FREECAD ASSEMBLY — COMPONENT RECIPES ("row")

This assembly document has 14 components, labeled P0..P13 below (a component is one placed body or linked part). 12 of them carry a construction recipe — the FreeCAD feature program that regenerates the part from scratch, quoted from this document or its linked companion documents; the rest are supplied as boundary geometry only. No exploded tour is included for this assembly.
COMPONENT P0 — recipe-attached ("BusBoard", a linked part whose construction recipe lives in a companion FreeCAD document of the same project; that document's serialized recipe follows).
Construction recipe (the companion document, serialized — sketch geometry with constraints, then the solid features built on it; lengths are millimeters unless a unit is written):

FCSTD DOCUMENT  (FreeCAD 1.0R38641 +468 (Git))
Label: doepfer_bus_board_v6
License: All rights reserved
LicenseURL: https://en.wikipedia.org/wiki/All_rights_reserved
objects: Sketcher::SketchObject×1, PartDesign::Pad×1, PartDesign::Body×1
note: 6 computed .brp shape members not serialized (recipe doc carries the construction recipe); baked Part::Feature solids carry a one-line shape summary decoded from their .brp

FEATURE [Sketcher::SketchObject] Sketch
  ArcFitTolerance = 1e-06
  AttachmentSupport = -> [XY_Plane]
  FullyConstrained = true
  MakeInternals = false
  MapMode = 5
  sketch-geometry (19):
    g0: LineSegment StartX=0 StartY=41.91 StartZ=0 EndX=0 EndY=0 EndZ=0
    g1: LineSegment StartX=0 StartY=0 StartZ=0 EndX=391.16 EndY=0 EndZ=0
    g2: LineSegment StartX=391.16 StartY=0 StartZ=0 EndX=391.16 EndY=41.91 EndZ=0
    g3: LineSegment StartX=391.16 StartY=41.91 StartZ=0 EndX=0 EndY=41.91 EndZ=0
    g4: Circle CenterX=24.13 CenterY=3.175 CenterZ=0 NormalX=0 NormalY=0 NormalZ=1 AngleXU=0 Radius=1.5
    g5: Circle [constr] CenterX=49.53 CenterY=3.175 CenterZ=0 NormalX=0 NormalY=0 NormalZ=1 AngleXU=0 Radius=1.5
    g6: Circle CenterX=74.93 CenterY=3.175 CenterZ=0 NormalX=0 NormalY=0 NormalZ=1 AngleXU=0 Radius=1.5
    g7: Circle [constr] CenterX=100.33 CenterY=3.175 CenterZ=0 NormalX=0 NormalY=0 NormalZ=1 AngleXU=0 Radius=1.5
    g8: Circle CenterX=125.73 CenterY=3.175 CenterZ=0 NormalX=0 NormalY=0 NormalZ=1 AngleXU=0 Radius=1.5
    g9: Circle CenterX=176.53 CenterY=3.175 CenterZ=0 NormalX=0 NormalY=0 NormalZ=1 AngleXU=0 Radius=1.5
    g10: Circle [constr] CenterX=151.13 CenterY=3.175 CenterZ=0 NormalX=0 NormalY=0 NormalZ=1 AngleXU=0 Radius=1.5
    g11: LineSegment [constr] StartX=0 StartY=3.175 StartZ=0 EndX=391.16 EndY=3.175 EndZ=0
    g12: Circle CenterX=214.63 CenterY=3.175 CenterZ=0 NormalX=0 NormalY=0 NormalZ=1 AngleXU=0 Radius=1.5
    g13: Circle [constr] CenterX=240.03 CenterY=3.175 CenterZ=0 NormalX=0 NormalY=0 NormalZ=1 AngleXU=0 Radius=1.5
    g14: Circle CenterX=265.43 CenterY=3.175 CenterZ=0 NormalX=0 NormalY=0 NormalZ=1 AngleXU=0 Radius=1.5
    g15: Circle [constr] CenterX=290.83 CenterY=3.175 CenterZ=0 NormalX=0 NormalY=0 NormalZ=1 AngleXU=0 Radius=1.5
    g16: Circle CenterX=316.23 CenterY=3.175 CenterZ=0 NormalX=0 NormalY=0 NormalZ=1 AngleXU=0 Radius=1.5
    g17: Circle [constr] CenterX=341.63 CenterY=3.175 CenterZ=0 NormalX=0 NormalY=0 NormalZ=1 AngleXU=0 Radius=1.5
    g18: Circle CenterX=367.03 CenterY=3.175 CenterZ=0 NormalX=0 NormalY=0 NormalZ=1 AngleXU=0 Radius=1.5
  constraints (52):
    c: Coincident(g0,g1)
    c: Coincident(g1,g2)
    c: Coincident(g2,g3)
    c: Coincident(g3,g0)
    c: Vertical(g0)
    c: Vertical(g2)
    c: Horizontal(g1)
    c: Horizontal(g3)
    c: Coincident(g0,g-1)
    c: DistanceX(g1,g1) = 391.16
    c: DistanceY(g0,g0) = 41.91
    c: PointOnObject(g11,g0)
    c: PointOnObject(g11,g2)
    c: Horizontal(g11)
    c: DistanceY(g0,g11) = 3.175
    c: PointOnObject(g4,g11)
    c: PointOnObject(g5,g11)
    c: PointOnObject(g6,g11)
    c: PointOnObject(g7,g11)
    c: PointOnObject(g8,g11)
    c: PointOnObject(g9,g11)
    c: PointOnObject(g10,g11)
    c: DistanceX(g11,g4) = 24.13
    c: DistanceX(g4,g5) = 25.4
    c: DistanceX(g5,g6) = 25.4
    c: DistanceX(g6,g7) = 25.4
    c: Distance(g7,g8) = 25.4
    c: Distance(g8,g10) = 25.4
    c: DistanceX(g10,g9) = 25.4
    c: PointOnObject(g12,g11)
    c: PointOnObject(g13,g11)
    c: PointOnObject(g14,g11)
    c: PointOnObject(g15,g11)
    c: PointOnObject(g16,g11)
    c: PointOnObject(g17,g11)
    c: PointOnObject(g18,g11)
    c: DistanceX(g9,g12) = 38.1
    c: DistanceX(g12,g13) = 25.4
    c: DistanceX(g13,g14) = 25.4
    c: DistanceX(g14,g15) = 25.4
    c: DistanceX(g15,g16) = 25.4
    c: DistanceX(g16,g17) = 25.4
    c: DistanceX(g17,g18) = 25.4
    c: Diameter(g4) = 3  'HoleDiameter'
    c: Equal(g4, g5-g8) x4
    c: Equal(g4,g10)
    c: Equal(g4,g9)
    c: Equal(g4, g12-g15) x4
    c: Equal(g16,g4)
    c: Equal(g4,g17)
    c: Equal(g18,g4)
    c: DistanceX(g18,g11) = 24.13
FEATURE [PartDesign::Pad] Pad
  Direction = (0,0,1)
  Length = 1
  Length2 = 10
  Profile = -> Sketch
  ReferenceAxis = -> Sketch [N_Axis]
  Refine = true
  Suppressed = false
  Type = 0
FEATURE [PartDesign::Body] Body  label="BusBoard"
  AllowCompound = false
  Group = -> [Sketch,Pad]
  Origin = -> Origin
  Tip = -> Pad
COMPONENT P1 — recipe-attached ("FrameBracket", a linked part whose construction recipe lives in a companion FreeCAD document of the same project; that document's serialized recipe follows).
Construction recipe (the companion document, serialized — sketch geometry with constraints, then the solid features built on it; lengths are millimeters unless a unit is written):

FCSTD DOCUMENT  (FreeCAD 1.0R38641 +468 (Git))
Label: frame_bracket
License: All rights reserved
LicenseURL: https://en.wikipedia.org/wiki/All_rights_reserved
objects: PartDesign::SubShapeBinder×1, Sketcher::SketchObject×1, PartDesign::Pad×1, PartDesign::Body×1
note: 7 computed .brp shape members not serialized (recipe doc carries the construction recipe); baked Part::Feature solids carry a one-line shape summary decoded from their .brp
EXTERNAL_REF file=panel_side.FCStd obj=Body001
EXTERNAL_REF file=dimensions.FCStd obj=VarSet

FEATURE [PartDesign::SubShapeBinder] Binder  label="SidePanelBinder"
  BindCopyOnChange = 0
  BindMode = 0
  ClaimChildren = false
  Context = -> Body [Binder.]
  Fuse = false
  MakeFace = true
  OffsetFill = false
  OffsetIntersection = false
  OffsetJoinType = 0
  OffsetOpenResult = false
  PartialLoad = false
  Refine = true
  Relative = true
  Support = -> [<external panel_side.FCStd>#Body001]
  _Version = 2
FEATURE [Sketcher::SketchObject] Sketch
  ArcFitTolerance = 1e-06
  AttachmentSupport = -> [Binder]
  ExternalGeometry = -> [Binder]
  FullyConstrained = true
  MakeInternals = false
  MapMode = 5
  Placement = pos=(-1.8542,0,0) rot=(0.57735,0.57735,0.57735;2.0944rad)
  expr: Constraints[114] = dimensions#VarSet.MaxAngle / 2
  expr: Constraints[115] = dimensions#VarSet.MaxAngle / 2
  expr: Constraints[63] = dimensions#VarSet.FrameHoleDiameter
  sketch-geometry (47):
    g0: Circle CenterX=56.923 CenterY=-56.25 CenterZ=0 NormalX=0 NormalY=0 NormalZ=1 AngleXU=0 Radius=3
    g1: Circle CenterX=73.177 CenterY=-56.25 CenterZ=0 NormalX=0 NormalY=0 NormalZ=1 AngleXU=0 Radius=3
    g2: ArcOfCircle CenterX=56.923 CenterY=-56.25 CenterZ=0 NormalX=0 NormalY=0 NormalZ=1 AngleXU=0 Radius=8 StartAngle=3.09569 EndAngle=4.71239
    g3: ArcOfCircle CenterX=73.177 CenterY=-56.25 CenterZ=0 NormalX=0 NormalY=0 NormalZ=1 AngleXU=0 Radius=8 StartAngle=6.23728 EndAngle=7.85398
    g4: ArcOfCircle CenterX=4.7e-14 CenterY=11.2 CenterZ=0 NormalX=0 NormalY=0 NormalZ=1 AngleXU=0 Radius=18.527 StartAngle=3.14159 EndAngle=3.33794
    g5: ArcOfCircle CenterX=-10.527 CenterY=11.2 CenterZ=0 NormalX=0 NormalY=0 NormalZ=1 AngleXU=0 Radius=8 StartAngle=6.23728 EndAngle=9.42478
    g6: ArcOfCircle CenterX=4.7e-14 CenterY=11.2 CenterZ=0 NormalX=0 NormalY=0 NormalZ=1 AngleXU=0 Radius=13.527 StartAngle=3.14159 EndAngle=3.33794
    g7: ArcOfCircle CenterX=-10.3247 CenterY=9.14628 CenterZ=0 NormalX=0 NormalY=0 NormalZ=1 AngleXU=0 Radius=3 StartAngle=3.33794 EndAngle=6.47953
    g8: ArcOfCircle CenterX=-10.527 CenterY=11.2 CenterZ=0 NormalX=0 NormalY=0 NormalZ=1 AngleXU=0 Radius=3 StartAngle=0 EndAngle=3.14159
    g9: ArcOfCircle CenterX=4.7e-14 CenterY=11.2 CenterZ=0 NormalX=0 NormalY=0 NormalZ=1 AngleXU=0 Radius=7.527 StartAngle=3.14159 EndAngle=3.33794
    g10: ArcOfCircle CenterX=4.67e-14 CenterY=-123.7 CenterZ=0 NormalX=0 NormalY=0 NormalZ=1 AngleXU=0 Radius=148.627 StartAngle=6.08684 EndAngle=6.28319
    g11: ArcOfCircle CenterX=137.925 CenterY=-151.135 CenterZ=0 NormalX=0 NormalY=0 NormalZ=1 AngleXU=0 Radius=8 StartAngle=2.94524 EndAngle=6.08684
    g12: ArcOfCircle CenterX=4.67e-14 CenterY=-123.7 CenterZ=0 NormalX=0 NormalY=0 NormalZ=1 AngleXU=0 Radius=132.627 StartAngle=6.08684 EndAngle=6.28648
    g13: ArcOfCircle CenterX=4.67e-14 CenterY=-123.7 CenterZ=0 NormalX=0 NormalY=0 NormalZ=1 AngleXU=0 Radius=143.627 StartAngle=6.08684 EndAngle=6.28319
    g14: ArcOfCircle CenterX=140.627 CenterY=-123.7 CenterZ=0 NormalX=0 NormalY=0 NormalZ=1 AngleXU=0 Radius=3 StartAngle=3e-16 EndAngle=3.14159
    g15: ArcOfCircle CenterX=137.925 CenterY=-151.135 CenterZ=0 NormalX=0 NormalY=0 NormalZ=1 AngleXU=0 Radius=3 StartAngle=2.94524 EndAngle=6.08684
    g16: ArcOfCircle CenterX=4.67e-14 CenterY=-123.7 CenterZ=0 NormalX=0 NormalY=0 NormalZ=1 AngleXU=0 Radius=137.627 StartAngle=6.08684 EndAngle=6.28319
    g17: LineSegment [constr] StartX=4.67e-14 StartY=-123.7 StartZ=0 EndX=148.627 EndY=-123.7 EndZ=0
    g18: LineSegment [constr] StartX=4.7e-14 StartY=11.2 StartZ=0 EndX=-18.527 EndY=11.2 EndZ=0
    g19: LineSegment [constr] StartX=56.923 StartY=-56.25 StartZ=0 EndX=-10.527 EndY=11.2 EndZ=0
    g20: LineSegment [constr] StartX=73.177 StartY=-56.25 StartZ=0 EndX=140.627 EndY=-123.7 EndZ=0
    g21: LineSegment [constr] StartX=73.177 StartY=-59.25 StartZ=0 EndX=76.177 EndY=-59.25 EndZ=0
    g22: LineSegment StartX=81.5188 StartY=-57.5207 StartZ=0 EndX=139.356 EndY=-115.358 EndZ=0
    g23: LineSegment StartX=74.4574 StartY=-64.6015 StartZ=0 EndX=132.275 EndY=-122.419 EndZ=0
    g24: LineSegment StartX=-7.42456 StartY=1.02649 StartZ=0 EndX=48.5812 EndY=-54.9793 EndZ=0
    g25: LineSegment StartX=55.6426 StartY=-47.8985 StartZ=0 EndX=-2.18522 EndY=9.92929 EndZ=0
    g26: ArcOfCircle CenterX=47.7327 CenterY=-55.8278 CenterZ=0 NormalX=0 NormalY=0 NormalZ=1 AngleXU=0 Radius=1.2 StartAngle=6.23728 EndAngle=7.06858
    g27: LineSegment StartX=56.4911 StartY=-48.25 StartZ=0 EndX=73.177 EndY=-48.25 EndZ=0
    g28: ArcOfCircle CenterX=56.4911 CenterY=-47.05 CenterZ=0 NormalX=0 NormalY=0 NormalZ=1 AngleXU=0 Radius=1.2 StartAngle=3.92699 EndAngle=4.71239
    g29: ArcOfCircle CenterX=82.3673 CenterY=-56.6722 CenterZ=0 NormalX=0 NormalY=0 NormalZ=1 AngleXU=0 Radius=1.2 StartAngle=3.09569 EndAngle=3.92699
    g30: ArcOfCircle CenterX=73.6089 CenterY=-65.45 CenterZ=0 NormalX=0 NormalY=0 NormalZ=1 AngleXU=0 Radius=1.2 StartAngle=0.785398 EndAngle=1.5708
    g31: LineSegment StartX=56.923 StartY=-64.25 StartZ=0 EndX=73.6089 EndY=-64.25 EndZ=0
    g32: ArcOfCircle CenterX=140.627 CenterY=-123.7 CenterZ=0 NormalX=0 NormalY=0 NormalZ=1 AngleXU=0 Radius=8 StartAngle=2e-16 EndAngle=1.6167
    g33: ArcOfCircle CenterX=140.205 CenterY=-114.51 CenterZ=0 NormalX=0 NormalY=0 NormalZ=1 AngleXU=0 Radius=1.2 StartAngle=3.92699 EndAngle=4.75829
    g34: ArcOfCircle CenterX=131.426 CenterY=-123.267 CenterZ=0 NormalX=0 NormalY=0 NormalZ=1 AngleXU=0 Radius=1.2 StartAngle=0.00329147 EndAngle=0.785398
    g35: ArcOfCircle CenterX=-10.3247 CenterY=9.14628 CenterZ=0 NormalX=0 NormalY=0 NormalZ=1 AngleXU=0 Radius=8 StartAngle=3.33794 EndAngle=4.93728
    g36: ArcOfCircle CenterX=-8.27309 CenterY=0.177963 CenterZ=0 NormalX=0 NormalY=0 NormalZ=1 AngleXU=0 Radius=1.2 StartAngle=0.785398 EndAngle=1.79569
    g37: ArcOfCircle CenterX=-1.33669 CenterY=10.7778 CenterZ=0 NormalX=0 NormalY=0 NormalZ=1 AngleXU=0 Radius=1.2 StartAngle=3.09569 EndAngle=3.92699
    g38: LineSegment [constr] StartX=4.7e-14 StartY=11.2 StartZ=0 EndX=4.7e-14 EndY=10 EndZ=0
    g39: LineSegment [constr] StartX=4.67e-14 StartY=-123.7 StartZ=0 EndX=4.67e-14 EndY=-122.5 EndZ=0
    g40: LineSegment [constr] StartX=53.923 StartY=-53.25 StartZ=0 EndX=56.923 EndY=-53.25 EndZ=0
    g41: LineSegment [constr] StartX=56.923 StartY=-53.25 StartZ=0 EndX=56.923 EndY=-56.25 EndZ=0
    g42: LineSegment [constr] StartX=73.177 StartY=-56.25 StartZ=0 EndX=73.177 EndY=-59.25 EndZ=0
    g43: LineSegment [constr] StartX=103.366 StartY=-93.5105 StartZ=0 EndX=106.902 EndY=-89.975 EndZ=0
    g44: LineSegment [constr] StartX=106.902 StartY=-89.975 StartZ=0 EndX=110.438 EndY=-86.4395 EndZ=0
    g45: LineSegment [constr] StartX=19.6625 StartY=-26.0605 StartZ=0 EndX=23.198 EndY=-22.525 EndZ=0
    g46: LineSegment [constr] StartX=23.198 StartY=-22.525 StartZ=0 EndX=26.7335 EndY=-18.9895 EndZ=0
  constraints (116):
    c: Coincident(g2,g0)
    c: Coincident(g3,g1)
    c: Tangent(g4,g5) = -1.5708
    c: Tangent(g4,g35) = -1.5708
    c: Coincident(g6,g9)
    c: Tangent(g9,g8) = 1.5708
    c: Tangent(g9,g7) = 1.5708
    c: Tangent(g6,g8) = -1.5708
    c: Tangent(g6,g7) = -1.5708
    c: Coincident(g6,g4)
    c: Coincident(g7,g35)
    c: Coincident(g10,g12)
    c: Tangent(g12,g11) = 1.5708
    c: Tangent(g10,g32) = -1.5708
    c: Tangent(g10,g11) = -1.5708
    c: Coincident(g13,g16)
    c: Tangent(g16,g15) = 1.5708
    c: Tangent(g16,g14) = 1.5708
    c: Tangent(g13,g15) = -1.5708
    c: Tangent(g13,g14) = -1.5708
    c: Coincident(g13,g10)
    c: Coincident(g14,g32)
    c: Coincident(g17,g10)
    c: Equal(g0,g1)
    c: Equal(g1,g14)
    c: Equal(g7,g0)
    c: Coincident(g18,g4)
    c: Horizontal(g18)
    c: Coincident(g4,g18)
    c: Coincident(g19,g0)
    c: Coincident(g5,g19)
    c: Coincident(g20,g1)
    c: PointOnObject(g21,g1)
    c: PointOnObject(g21,g20)
    c: Horizontal(g21)
    c: Coincident(g20,g32)
    c: Parallel(g23,g20)
    c: Parallel(g20,g22)
    c: Parallel(g24,g19)
    c: Parallel(g19,g25)
    c: Tangent(g26,g2) = 1.5708
    c: Tangent(g24,g26) = 1.5708
    c: Horizontal(g27)
    c: Tangent(g28,g27) = -1.5708
    c: Tangent(g25,g28) = 1.5708
    c: Tangent(g29,g3) = 1.5708
    c: Tangent(g29,g22) = -1.5708
    c: Tangent(g23,g30) = 1.5708
    c: Horizontal(g31)
    c: Tangent(g3,g27) = 1.5708
    c: Tangent(g2,g31) = -1.5708
    c: Distance(g25,g24) = 10
    c: Distance(g22,g23) = 10
    c: Tangent(g30,g31) = 1.5708
    c: Tangent(g33,g32) = 1.5708
    c: Tangent(g33,g22) = -1.5708
    c: Tangent(g34,g23) = 1.5708
    c: Coincident(g17,g10)
    c: Tangent(g35,g36) = 1.5708
    c: Tangent(g36,g24) = 1.5708
    c: Tangent(g37,g25) = 1.5708
    c: Coincident(g8,g5)
    c: Tangent(g12,g34) = -1.5708
    c: Diameter(g0) = 6
    c: Coincident(g38,g4)
    c: Coincident(g39,g10)
    c: Horizontal(g17)
    c: Coincident(g15,g11)
    c: Equal(g39,g38)
    c: Distance(g2,g0) = 5
    c: Equal(g2,g3)
    c: Equal(g29,g30)
    c: Equal(g30,g26)
    c: Equal(g28,g26)
    c: Distance(g15,g11) = 5
    c: Distance(g5,g8) = 5
    c: Distance(g38,g38) = 1.2
    c: Tangent(g37,g5) = 1.5708
    c: Equal(g34,g33)
    c: Equal(g33,g30)
    c: PointOnObject(g40,g19)
    c: PointOnObject(g40,g0)
    c: Horizontal(g40)
    c: Coincident(g41,g40)
    c: Coincident(g41,g0)
    c: Vertical(g41)
    c: Equal(g41,g40)
    c: Coincident(g42,g1)
    c: Coincident(g42,g21)
    c: Vertical(g42)
    c: Equal(g42,g21)
    c: Equal(g28,g37)
    c: Equal(g37,g36)
    c: Radius(g30) = 1.2
    c: PointOnObject(g43,g23)
    c: Coincident(g44,g43)
    c: PointOnObject(g44,g22)
    c: Perpendicular(g43,g23)
    c: Perpendicular(g22,g44)
    c: Equal(g43,g44)
    c: PointOnObject(g45,g24)
    c: PointOnObject(g46,g25)
    c: Perpendicular(g25,g46)
    c: Perpendicular(g24,g45)
    c: Coincident(g46,g45)
    c: Equal(g46,g45)
    c: Symmetric(g1,g14,g43)
    c: Symmetric(g0,g5,g45)
    c: Coincident(g1,g-4)
    c: Coincident(g0,g-3)
    c: Coincident(g39,g-5)
    c: Vertical(g39)
    c: Coincident(g38,g-6)
    c: Vertical(g38)
    c: Angle(g10) = 0.19635
    c: Angle(g4) = 0.19635
FEATURE [PartDesign::Pad] Pad
  Direction = (1,0,0)
  Length = 3.175
  Length2 = 10
  Profile = -> Sketch
  ReferenceAxis = -> Sketch [N_Axis]
  Refine = true
  Reversed = true
  Suppressed = false
  Type = 0
  expr: Length = <<dimensions>>#VarSet.FrameTotalThickness
FEATURE [PartDesign::Body] Body  label="FrameBracket"
  AllowCompound = false
  Group = -> [Sketch,Pad,Binder]
  Origin = -> Origin
  Tip = -> Pad
COMPONENT P2 — same part as P1; its construction recipe is shown at P1.
COMPONENT P3 — same part as P1; its construction recipe is shown at P1.
COMPONENT P4 — same part as P1; its construction recipe is shown at P1.
COMPONENT P5 — recipe-attached ("FramePanelSpacer", a linked part whose construction recipe lives in a companion FreeCAD document of the same project; that document's serialized recipe follows).
Construction recipe (the companion document, serialized — sketch geometry with constraints, then the solid features built on it; lengths are millimeters unless a unit is written):

FCSTD DOCUMENT  (FreeCAD 1.0R38641 +468 (Git))
Label: frame_panel_spacer
License: All rights reserved
LicenseURL: https://en.wikipedia.org/wiki/All_rights_reserved
objects: PartDesign::SubShapeBinder×2, Sketcher::SketchObject×1, PartDesign::Pad×1, PartDesign::Body×1
note: 8 computed .brp shape members not serialized (recipe doc carries the construction recipe); baked Part::Feature solids carry a one-line shape summary decoded from their .brp
EXTERNAL_REF file=panel_side.FCStd obj=Body001
EXTERNAL_REF file=dimensions.FCStd obj=VarSet
EXTERNAL_REF file=frame_bracket.FCStd obj=Body

FEATURE [PartDesign::SubShapeBinder] Binder  label="SidePanelBinder"
  BindCopyOnChange = 0
  BindMode = 0
  ClaimChildren = false
  Context = -> Body [Binder.]
  Fuse = false
  MakeFace = true
  OffsetFill = false
  OffsetIntersection = false
  OffsetJoinType = 0
  OffsetOpenResult = false
  PartialLoad = false
  Refine = true
  Relative = true
  Support = -> [<external panel_side.FCStd>#Body001]
  _Version = 2
FEATURE [PartDesign::SubShapeBinder] Binder001  label="BracketBinder"
  BindCopyOnChange = 0
  BindMode = 0
  ClaimChildren = false
  Context = -> Body [Binder001.]
  Fuse = false
  MakeFace = true
  OffsetFill = false
  OffsetIntersection = false
  OffsetJoinType = 0
  OffsetOpenResult = false
  PartialLoad = false
  Refine = true
  Relative = true
  Support = -> [<external frame_bracket.FCStd>#Body]
  _Version = 2
FEATURE [Sketcher::SketchObject] Sketch
  ArcFitTolerance = 1e-06
  AttachmentSupport = -> [Binder]
  ExternalGeometry = -> [Binder,Binder001]
  FullyConstrained = true
  MakeInternals = false
  MapMode = 5
  Placement = pos=(-1.8542,0,0) rot=(0.57735,0.57735,0.57735;2.0944rad)
  expr: Constraints[32] = dimensions#VarSet.FrameMinWidth
  expr: Constraints[33] = dimensions#VarSet.EnclosureCornerRadius
  expr: Constraints[41] = dimensions#VarSet.FrameHoleDiameter
  expr: Constraints[42] = dimensions#VarSet.FrameHoleDiameter / 2 + dimensions#VarSet.FrameMinWidth / 2
  sketch-geometry (21):
    g0: ArcOfCircle CenterX=56.923 CenterY=-56.25 CenterZ=0 NormalX=0 NormalY=0 NormalZ=1 AngleXU=0 Radius=8 StartAngle=1.5708 EndAngle=4.71239
    g1: ArcOfCircle CenterX=73.177 CenterY=-56.25 CenterZ=0 NormalX=0 NormalY=0 NormalZ=1 AngleXU=0 Radius=8 StartAngle=0.739492 EndAngle=1.5708
    g2: ArcOfCircle CenterX=79.9741 CenterY=-50.05 CenterZ=0 NormalX=0 NormalY=0 NormalZ=1 AngleXU=0 Radius=1.2 StartAngle=3.88109 EndAngle=4.71239
    g3: ArcOfCircle CenterX=73.177 CenterY=-56.25 CenterZ=0 NormalX=0 NormalY=0 NormalZ=1 AngleXU=0 Radius=8 StartAngle=4.71239 EndAngle=5.54369
    g4: ArcOfCircle CenterX=79.9741 CenterY=-62.45 CenterZ=0 NormalX=0 NormalY=0 NormalZ=1 AngleXU=0 Radius=1.2 StartAngle=1.5708 EndAngle=2.4021
    g5: ArcOfCircle CenterX=140.627 CenterY=-56.25 CenterZ=0 NormalX=0 NormalY=0 NormalZ=1 AngleXU=0 Radius=8 StartAngle=3.88109 EndAngle=8.68529
    g6: ArcOfCircle CenterX=133.83 CenterY=-62.45 CenterZ=0 NormalX=0 NormalY=0 NormalZ=1 AngleXU=0 Radius=1.2 StartAngle=0.739492 EndAngle=1.5708
    g7: ArcOfCircle CenterX=133.83 CenterY=-50.05 CenterZ=0 NormalX=0 NormalY=0 NormalZ=1 AngleXU=0 Radius=1.2 StartAngle=4.71239 EndAngle=5.54369
    g8: LineSegment StartX=56.923 StartY=-48.25 StartZ=0 EndX=73.177 EndY=-48.25 EndZ=0
    g9: LineSegment StartX=56.923 StartY=-64.25 StartZ=0 EndX=73.177 EndY=-64.25 EndZ=0
    g10: LineSegment StartX=79.9741 StartY=-61.25 StartZ=0 EndX=133.83 EndY=-61.25 EndZ=0
    g11: LineSegment StartX=79.9741 StartY=-51.25 StartZ=0 EndX=133.83 EndY=-51.25 EndZ=0
    g12: LineSegment [constr] StartX=56.923 StartY=-56.25 StartZ=0 EndX=140.627 EndY=-56.25 EndZ=0
    g13: LineSegment [constr] StartX=56.923 StartY=-48.25 StartZ=0 EndX=56.923 EndY=-64.25 EndZ=0
    g14: LineSegment [constr] StartX=73.177 StartY=-48.25 StartZ=0 EndX=73.177 EndY=-64.25 EndZ=0
    g15: Circle CenterX=56.923 CenterY=-56.25 CenterZ=0 NormalX=0 NormalY=0 NormalZ=1 AngleXU=0 Radius=3
    g16: Circle CenterX=73.177 CenterY=-56.25 CenterZ=0 NormalX=0 NormalY=0 NormalZ=1 AngleXU=0 Radius=3
    g17: Circle CenterX=140.627 CenterY=-56.25 CenterZ=0 NormalX=0 NormalY=0 NormalZ=1 AngleXU=0 Radius=3
    g18: LineSegment [constr] StartX=148.627 StartY=-123.7 StartZ=0 EndX=148.627 EndY=-56.25 EndZ=0
    g19: Circle [constr] CenterX=56.923 CenterY=-56.25 CenterZ=0 NormalX=0 NormalY=0 NormalZ=1 AngleXU=0 Radius=8
    g20: Circle [constr] CenterX=73.177 CenterY=-56.25 CenterZ=0 NormalX=0 NormalY=0 NormalZ=1 AngleXU=0 Radius=8
  constraints (51):
    c: Coincident(g3,g1)
    c: Coincident(g8,g0)
    c: Coincident(g8,g1)
    c: Horizontal(g8)
    c: Coincident(g9,g0)
    c: Coincident(g9,g3)
    c: Horizontal(g9)
    c: Horizontal(g11)
    c: Horizontal(g10)
    c: Tangent(g4,g3) = 1.5708
    c: Tangent(g2,g1) = 1.5708
    c: Tangent(g7,g5) = 1.5708
    c: Tangent(g5,g6) = 1.5708
    c: Coincident(g12,g0)
    c: Coincident(g12,g5)
    c: Horizontal(g12)
    c: Coincident(g13,g0)
    c: Coincident(g13,g0)
    c: Vertical(g13)
    c: PointOnObject(g0,g13)
    c: Coincident(g14,g1)
    c: Coincident(g14,g3)
    c: PointOnObject(g1,g14)
    c: Vertical(g14)
    c: Tangent(g11,g2) = -1.5708
    c: Tangent(g10,g4) = 1.5708
    c: Tangent(g7,g11) = -1.5708
    c: Tangent(g10,g6) = 1.5708
    c: Equal(g1,g5)
    c: Equal(g2,g7)
    c: Equal(g6,g4)
    c: Symmetric(g4,g2,g12)
    c: Distance(g10,g11) = 10
    c: Radius(g2) = 1.2
    c: Coincident(g0,g-3)
    c: Coincident(g1,g-4)
    c: Coincident(g15,g0)
    c: Coincident(g16,g1)
    c: Coincident(g17,g5)
    c: Equal(g17,g16)
    c: Equal(g16,g15)
    c: Diameter(g15) = 6
    c: Radius(g0) = 8
    c: Vertical(g18)
    c: Coincident(g-5,g18)
    c: Tangent(g18,g5) = -1.5708
    c: Coincident(g19,g0)
    c: Equal(g19,g0)
    c: Coincident(g20,g1)
    c: Equal(g20,g1)
    c: Distance(g19,g20) = 0.254
FEATURE [PartDesign::Pad] Pad
  Direction = (1,0,0)
  Length = 3.175
  Length2 = 10
  Profile = -> Sketch
  ReferenceAxis = -> Sketch [N_Axis]
  Refine = true
  Reversed = true
  Suppressed = false
  Type = 0
  expr: Length = <<dimensions>>#VarSet.FrameTotalThickness
FEATURE [PartDesign::Body] Body  label="FramePanelSpacer"
  AllowCompound = false
  Group = -> [Pad,Sketch,Binder,Binder001]
  Origin = -> Origin
  Tip = -> Pad
COMPONENT P6 — same part as P5; its construction recipe is shown at P5.
COMPONENT P7 — recipe-attached ("PanelBack", a linked part whose construction recipe lives in a companion FreeCAD document of the same project; that document's serialized recipe follows).
Construction recipe (the companion document, serialized — sketch geometry with constraints, then the solid features built on it; lengths are millimeters unless a unit is written):

FCSTD DOCUMENT  (FreeCAD 1.0R38641 +468 (Git))
Label: panel_back
License: All rights reserved
LicenseURL: https://en.wikipedia.org/wiki/All_rights_reserved
objects: PartDesign::SubShapeBinder×4, Sketcher::SketchObject×1, PartDesign::Pad×1, PartDesign::Body×1
note: 10 computed .brp shape members not serialized (recipe doc carries the construction recipe); baked Part::Feature solids carry a one-line shape summary decoded from their .brp
EXTERNAL_REF file=dimensions.FCStd obj=VarSet
EXTERNAL_REF file=../third_party/doepfer_bus_board_v6.FCStd obj=Sketch
EXTERNAL_REF file=panel_top_and_bottom.FCStd obj=Body
EXTERNAL_REF file=panel_side.FCStd obj=Body001
EXTERNAL_REF file=../third_party/doepfer_bus_board_v6.FCStd obj=Body
EXTERNAL_REF file=../third_party/doepfer_psu3.FCStd obj=Body

FEATURE [PartDesign::SubShapeBinder] Binder  label="BottomPanelBinder"
  BindCopyOnChange = 0
  BindMode = 0
  ClaimChildren = false
  Context = -> Body [Binder.]
  Fuse = false
  MakeFace = true
  OffsetFill = false
  OffsetIntersection = false
  OffsetJoinType = 0
  OffsetOpenResult = false
  PartialLoad = false
  Refine = true
  Relative = true
  Support = -> [<external panel_top_and_bottom.FCStd>#Body[Pad.]]
  _Version = 2
FEATURE [PartDesign::SubShapeBinder] Binder001  label="SidePanelBinder"
  BindCopyOnChange = 0
  BindMode = 0
  ClaimChildren = false
  Context = -> Body [Binder001.]
  Fuse = false
  MakeFace = true
  OffsetFill = false
  OffsetIntersection = false
  OffsetJoinType = 0
  OffsetOpenResult = false
  PartialLoad = false
  Refine = true
  Relative = true
  Support = -> [<external panel_side.FCStd>#Body001]
  _Version = 2
FEATURE [PartDesign::SubShapeBinder] Binder002  label="BusBoardBinder"
  BindCopyOnChange = 0
  BindMode = 0
  ClaimChildren = false
  Context = -> Body [Binder002.]
  Fuse = false
  MakeFace = true
  OffsetFill = false
  OffsetIntersection = false
  OffsetJoinType = 0
  OffsetOpenResult = false
  PartialLoad = false
  Placement = pos=(0,0,0) rot=(1,0,0;1.5708rad)
  Refine = true
  Relative = true
  Support = -> [<external ../third_party/doepfer_bus_board_v6.FCStd>#Body]
  _Version = 2
FEATURE [PartDesign::SubShapeBinder] Binder003  label="PsuBinder"
  BindCopyOnChange = 0
  BindMode = 0
  ClaimChildren = false
  Context = -> Body [Binder003.]
  Fuse = false
  MakeFace = true
  OffsetFill = false
  OffsetIntersection = false
  OffsetJoinType = 0
  OffsetOpenResult = false
  PartialLoad = false
  Placement = pos=(0,0,0) rot=(1,0,0;1.5708rad)
  Refine = true
  Relative = false
  Support = -> [<external ../third_party/doepfer_psu3.FCStd>#Body]
  _Version = 2
FEATURE [Sketcher::SketchObject] Sketch
  ArcFitTolerance = 1e-06
  AttachmentOffset = pos=(0,0,0.127) rot=(0,0,1;0rad)
  AttachmentSupport = -> [Binder001,Binder]
  ExternalGeometry = -> [Binder001,Binder,Binder002,Binder003]
  FullyConstrained = true
  MakeInternals = false
  MapMode = 5
  Placement = pos=(0,127.227,2.68e-14) rot=(1,0,0;1.5708rad)
  expr: .AttachmentOffset.Base.z = dimensions#VarSet.EnclosureFinishThickness
  expr: Constraints[189] = dimensions#VarSet.EnclosureFinishThickness
  expr: Constraints[288] = doepfer_bus_board_v6#Sketch.Constraints.HoleDiameter + 2 * dimensions#VarSet.EnclosureFinishThickness
  expr: Constraints[41] = 2 * <<dimensions>>#VarSet.EnclosureFinishThickness
  expr: Constraints[47] = dimensions#VarSet.EnclosureCornerRadius
  expr: Constraints[82] = <<dimensions>>#VarSet.FrameTotalThickness - 2 * <<dimensions>>#VarSet.EnclosureFinishThickness
  expr: Constraints[83] = dimensions#VarSet.FrameMinWidth + dimensions#VarSet.FrameHoleDiameter + 2 * dimensions#VarSet.FrameFinishThickness
  expr: Constraints[84] = dimensions#VarSet.FrameTotalThickness + 2 * dimensions#VarSet.EnclosureFinishThickness
  sketch-geometry (148):
    g0: LineSegment [constr] StartX=1e-15 StartY=-23.125 StartZ=0 EndX=1e-15 EndY=-23.379 EndZ=0
    g1: LineSegment [constr] StartX=9e-16 StartY=-89.121 StartZ=0 EndX=9e-16 EndY=-89.375 EndZ=0
    g2: LineSegment StartX=1e-15 StartY=-23.379 StartZ=0 EndX=-6.8772 EndY=-23.379 EndZ=0
    g3: LineSegment StartX=-8.0772 StartY=-24.579 StartZ=0 EndX=-8.0772 EndY=-87.921 EndZ=0
    g4: LineSegment StartX=-6.8772 StartY=-89.121 StartZ=0 EndX=9e-16 EndY=-89.121 EndZ=0
    g5: LineSegment StartX=1.2 StartY=-90.321 StartZ=0 EndX=1.2 EndY=-114.173 EndZ=0
    g6: LineSegment StartX=425.8 StartY=-114.173 StartZ=0 EndX=425.8 EndY=-90.321 EndZ=0
    g7: LineSegment StartX=427 StartY=-89.121 StartZ=0 EndX=433.877 EndY=-89.121 EndZ=0
    g8: LineSegment StartX=435.077 StartY=-87.921 StartZ=0 EndX=435.077 EndY=-24.579 EndZ=0
    g9: LineSegment StartX=433.877 StartY=-23.379 StartZ=0 EndX=427 EndY=-23.379 EndZ=0
    g10: LineSegment StartX=425.8 StartY=-22.179 StartZ=0 EndX=425.8 EndY=1.6729 EndZ=0
    g11: LineSegment StartX=1.2 StartY=1.6729 StartZ=0 EndX=1.2 EndY=-22.179 EndZ=0
    g12: ArcOfCircle CenterX=424.6 CenterY=1.6729 CenterZ=0 NormalX=0 NormalY=0 NormalZ=1 AngleXU=0 Radius=1.2 StartAngle=0 EndAngle=1.5708
    g13: ArcOfCircle CenterX=427 CenterY=-22.179 CenterZ=0 NormalX=0 NormalY=0 NormalZ=1 AngleXU=0 Radius=1.2 StartAngle=3.14159 EndAngle=4.71239
    g14: ArcOfCircle CenterX=433.877 CenterY=-24.579 CenterZ=0 NormalX=0 NormalY=0 NormalZ=1 AngleXU=0 Radius=1.2 StartAngle=8e-16 EndAngle=1.5708
    g15: ArcOfCircle CenterX=433.877 CenterY=-87.921 CenterZ=0 NormalX=0 NormalY=0 NormalZ=1 AngleXU=0 Radius=1.2 StartAngle=4.71239 EndAngle=6.28319
    g16: ArcOfCircle CenterX=427 CenterY=-90.321 CenterZ=0 NormalX=0 NormalY=0 NormalZ=1 AngleXU=0 Radius=1.2 StartAngle=1.5708 EndAngle=3.14159
    g17: ArcOfCircle CenterX=424.6 CenterY=-114.173 CenterZ=0 NormalX=0 NormalY=0 NormalZ=1 AngleXU=0 Radius=1.2 StartAngle=4.71239 EndAngle=6.28319
    g18: ArcOfCircle CenterX=2.4 CenterY=-114.173 CenterZ=0 NormalX=0 NormalY=0 NormalZ=1 AngleXU=0 Radius=1.2 StartAngle=3.14159 EndAngle=4.71239
    g19: ArcOfCircle CenterX=9e-16 CenterY=-90.321 CenterZ=0 NormalX=0 NormalY=0 NormalZ=1 AngleXU=0 Radius=1.2 StartAngle=2.6e-15 EndAngle=1.5708
    g20: ArcOfCircle CenterX=-6.8772 CenterY=-87.921 CenterZ=0 NormalX=0 NormalY=0 NormalZ=1 AngleXU=0 Radius=1.2 StartAngle=3.14159 EndAngle=4.71239
    g21: ArcOfCircle CenterX=-6.8772 CenterY=-24.579 CenterZ=0 NormalX=0 NormalY=0 NormalZ=1 AngleXU=0 Radius=1.2 StartAngle=1.5708 EndAngle=3.14159
    g22: ArcOfCircle CenterX=1.2e-15 CenterY=-22.179 CenterZ=0 NormalX=0 NormalY=0 NormalZ=1 AngleXU=0 Radius=1.2 StartAngle=4.71239 EndAngle=6.28319
    g23: ArcOfCircle CenterX=2.4 CenterY=1.6729 CenterZ=0 NormalX=0 NormalY=0 NormalZ=1 AngleXU=0 Radius=1.2 StartAngle=1.5708 EndAngle=3.14159
    g24: ArcOfCircle CenterX=-3.4417 CenterY=-48.25 CenterZ=0 NormalX=0 NormalY=0 NormalZ=1 AngleXU=0 Radius=1.7145 StartAngle=8e-16 EndAngle=3.14159
    g25: ArcOfCircle CenterX=-3.4417 CenterY=-64.25 CenterZ=0 NormalX=0 NormalY=0 NormalZ=1 AngleXU=0 Radius=1.7145 StartAngle=3.14159 EndAngle=6.28319
    g26: LineSegment StartX=-1.7272 StartY=-48.25 StartZ=0 EndX=-1.7272 EndY=-64.25 EndZ=0
    g27: LineSegment StartX=-5.1562 StartY=-48.25 StartZ=0 EndX=-5.1562 EndY=-64.25 EndZ=0
    g28: LineSegment [constr] StartX=-3.4417 StartY=-48.25 StartZ=0 EndX=-3.4417 EndY=-23.379 EndZ=0
    g29: LineSegment [constr] StartX=-3.4417 StartY=-64.25 StartZ=0 EndX=-3.4417 EndY=-89.121 EndZ=0
    g30: LineSegment [constr] StartX=430.442 StartY=-23.379 StartZ=0 EndX=430.442 EndY=-48.25 EndZ=0
    g31: LineSegment [constr] StartX=430.442 StartY=-89.121 StartZ=0 EndX=430.442 EndY=-64.25 EndZ=0
    g32: ArcOfCircle CenterX=430.442 CenterY=-48.25 CenterZ=0 NormalX=0 NormalY=0 NormalZ=1 AngleXU=0 Radius=1.7145 StartAngle=-1.8e-15 EndAngle=3.14159
    g33: ArcOfCircle CenterX=430.442 CenterY=-64.25 CenterZ=0 NormalX=0 NormalY=0 NormalZ=1 AngleXU=0 Radius=1.7145 StartAngle=3.14159 EndAngle=6.28319
    g34: LineSegment StartX=432.156 StartY=-48.25 StartZ=0 EndX=432.156 EndY=-64.25 EndZ=0
    g35: LineSegment StartX=428.727 StartY=-48.25 StartZ=0 EndX=428.727 EndY=-64.25 EndZ=0
    g36: LineSegment [constr] StartX=-8.0772 StartY=-48.25 StartZ=0 EndX=-5.1562 EndY=-48.25 EndZ=0
    g37: LineSegment [constr] StartX=432.156 StartY=-48.25 StartZ=0 EndX=435.077 EndY=-48.25 EndZ=0
    g38: LineSegment StartX=72.679 StartY=2.8729 StartZ=0 EndX=2.4 EndY=2.8729 EndZ=0
    g39: LineSegment StartX=139.621 StartY=4.0729 StartZ=0 EndX=139.621 EndY=5.9271 EndZ=0
    g40: LineSegment StartX=138.421 StartY=7.1271 StartZ=0 EndX=75.079 EndY=7.1271 EndZ=0
    g41: LineSegment StartX=73.879 StartY=5.9271 StartZ=0 EndX=73.879 EndY=4.0729 EndZ=0
    g42: ArcOfCircle CenterX=72.679 CenterY=4.0729 CenterZ=0 NormalX=0 NormalY=0 NormalZ=1 AngleXU=0 Radius=1.2 StartAngle=4.71239 EndAngle=6.28319
    g43: ArcOfCircle CenterX=75.079 CenterY=5.9271 CenterZ=0 NormalX=0 NormalY=0 NormalZ=1 AngleXU=0 Radius=1.2 StartAngle=1.5708 EndAngle=3.14159
    g44: ArcOfCircle CenterX=138.421 CenterY=5.9271 CenterZ=0 NormalX=0 NormalY=0 NormalZ=1 AngleXU=0 Radius=1.2 StartAngle=1e-16 EndAngle=1.5708
    g45: ArcOfCircle CenterX=140.821 CenterY=4.0729 CenterZ=0 NormalX=0 NormalY=0 NormalZ=1 AngleXU=0 Radius=1.2 StartAngle=3.14159 EndAngle=4.71239
    g46: LineSegment StartX=353.121 StartY=4.0729 StartZ=0 EndX=353.121 EndY=5.9271 EndZ=0
    g47: LineSegment StartX=351.921 StartY=7.1271 StartZ=0 EndX=288.579 EndY=7.1271 EndZ=0
    g48: LineSegment StartX=287.379 StartY=5.9271 StartZ=0 EndX=287.379 EndY=4.0729 EndZ=0
    g49: ArcOfCircle CenterX=286.179 CenterY=4.0729 CenterZ=0 NormalX=0 NormalY=0 NormalZ=1 AngleXU=0 Radius=1.2 StartAngle=4.71239 EndAngle=6.28319
    g50: ArcOfCircle CenterX=288.579 CenterY=5.9271 CenterZ=0 NormalX=0 NormalY=0 NormalZ=1 AngleXU=0 Radius=1.2 StartAngle=1.5708 EndAngle=3.14159
    g51: ArcOfCircle CenterX=351.921 CenterY=5.9271 CenterZ=0 NormalX=0 NormalY=0 NormalZ=1 AngleXU=0 Radius=1.2 StartAngle=3e-16 EndAngle=1.5708
    g52: ArcOfCircle CenterX=354.321 CenterY=4.0729 CenterZ=0 NormalX=0 NormalY=0 NormalZ=1 AngleXU=0 Radius=1.2 StartAngle=3.14159 EndAngle=4.71239
    g53: LineSegment StartX=424.6 StartY=2.8729 StartZ=0 EndX=354.321 EndY=2.8729 EndZ=0
    g54: LineSegment StartX=2.4 StartY=-115.373 StartZ=0 EndX=72.679 EndY=-115.373 EndZ=0
    g55: LineSegment StartX=73.879 StartY=-116.573 StartZ=0 EndX=73.879 EndY=-118.427 EndZ=0
    g56: LineSegment StartX=75.079 StartY=-119.627 StartZ=0 EndX=138.421 EndY=-119.627 EndZ=0
    g57: LineSegment StartX=139.621 StartY=-118.427 StartZ=0 EndX=139.621 EndY=-116.573 EndZ=0
    g58: LineSegment StartX=140.821 StartY=-115.373 StartZ=0 EndX=286.179 EndY=-115.373 EndZ=0
    g59: LineSegment StartX=287.379 StartY=-116.573 StartZ=0 EndX=287.379 EndY=-118.427 EndZ=0
    g60: LineSegment StartX=288.579 StartY=-119.627 StartZ=0 EndX=351.921 EndY=-119.627 EndZ=0
    g61: ArcOfCircle CenterX=351.921 CenterY=-118.427 CenterZ=0 NormalX=0 NormalY=0 NormalZ=1 AngleXU=0 Radius=1.2 StartAngle=4.71239 EndAngle=6.28319
    g62: ArcOfCircle CenterX=288.579 CenterY=-118.427 CenterZ=0 NormalX=0 NormalY=0 NormalZ=1 AngleXU=0 Radius=1.2 StartAngle=3.14159 EndAngle=4.71239
    g63: ArcOfCircle CenterX=286.179 CenterY=-116.573 CenterZ=0 NormalX=0 NormalY=0 NormalZ=1 AngleXU=0 Radius=1.2 StartAngle=2.3e-15 EndAngle=1.5708
    g64: ArcOfCircle CenterX=140.821 CenterY=-116.573 CenterZ=0 NormalX=0 NormalY=0 NormalZ=1 AngleXU=0 Radius=1.2 StartAngle=1.5708 EndAngle=3.14159
    g65: ArcOfCircle CenterX=138.421 CenterY=-118.427 CenterZ=0 NormalX=0 NormalY=0 NormalZ=1 AngleXU=0 Radius=1.2 StartAngle=4.71239 EndAngle=6.28319
    g66: ArcOfCircle CenterX=75.079 CenterY=-118.427 CenterZ=0 NormalX=0 NormalY=0 NormalZ=1 AngleXU=0 Radius=1.2 StartAngle=3.14159 EndAngle=4.71239
    g67: ArcOfCircle CenterX=72.679 CenterY=-116.573 CenterZ=0 NormalX=0 NormalY=0 NormalZ=1 AngleXU=0 Radius=1.2 StartAngle=5.1e-15 EndAngle=1.5708
    g68: LineSegment StartX=353.121 StartY=-118.427 StartZ=0 EndX=353.121 EndY=-116.573 EndZ=0
    g69: ArcOfCircle CenterX=354.321 CenterY=-116.573 CenterZ=0 NormalX=0 NormalY=0 NormalZ=1 AngleXU=0 Radius=1.2 StartAngle=1.5708 EndAngle=3.14159
    g70: LineSegment StartX=354.321 StartY=-115.373 StartZ=0 EndX=424.6 EndY=-115.373 EndZ=0
    g71: LineSegment [constr] StartX=73.625 StartY=4.0729 StartZ=0 EndX=73.879 EndY=4.0729 EndZ=0
    g72: LineSegment [constr] StartX=139.621 StartY=4.0729 StartZ=0 EndX=139.875 EndY=4.0729 EndZ=0
    g73: LineSegment [constr] StartX=287.125 StartY=4.0729 StartZ=0 EndX=287.379 EndY=4.0729 EndZ=0
    g74: LineSegment [constr] StartX=353.121 StartY=4.0729 StartZ=0 EndX=353.375 EndY=4.0729 EndZ=0
    g75: Circle CenterX=194.45 CenterY=-74.03 CenterZ=0 NormalX=0 NormalY=0 NormalZ=1 AngleXU=0 Radius=1.627
    g76: Circle CenterX=232.55 CenterY=-74.03 CenterZ=0 NormalX=0 NormalY=0 NormalZ=1 AngleXU=0 Radius=1.627
    g77: Circle CenterX=283.35 CenterY=-74.03 CenterZ=0 NormalX=0 NormalY=0 NormalZ=1 AngleXU=0 Radius=1.627
    g78: Circle CenterX=334.15 CenterY=-74.03 CenterZ=0 NormalX=0 NormalY=0 NormalZ=1 AngleXU=0 Radius=1.627
    g79: Circle CenterX=384.95 CenterY=-74.03 CenterZ=0 NormalX=0 NormalY=0 NormalZ=1 AngleXU=0 Radius=1.627
    g80: Circle CenterX=143.65 CenterY=-74.03 CenterZ=0 NormalX=0 NormalY=0 NormalZ=1 AngleXU=0 Radius=1.627
    g81: Circle CenterX=92.85 CenterY=-74.03 CenterZ=0 NormalX=0 NormalY=0 NormalZ=1 AngleXU=0 Radius=1.627
    g82: Circle CenterX=42.05 CenterY=-74.03 CenterZ=0 NormalX=0 NormalY=0 NormalZ=1 AngleXU=0 Radius=1.627
    g83: LineSegment [constr] StartX=42.05 StartY=-74.03 StartZ=0 EndX=92.85 EndY=-74.03 EndZ=0
    g84: LineSegment [constr] StartX=92.85 StartY=-74.03 StartZ=0 EndX=143.65 EndY=-74.03 EndZ=0
    g85: LineSegment [constr] StartX=143.65 StartY=-74.03 StartZ=0 EndX=194.45 EndY=-74.03 EndZ=0
    g86: LineSegment [constr] StartX=194.45 StartY=-74.03 StartZ=0 EndX=232.55 EndY=-74.03 EndZ=0
    g87: LineSegment [constr] StartX=232.55 StartY=-74.03 StartZ=0 EndX=283.35 EndY=-74.03 EndZ=0
    g88: LineSegment [constr] StartX=283.35 StartY=-74.03 StartZ=0 EndX=334.15 EndY=-74.03 EndZ=0
    g89: LineSegment [constr] StartX=334.15 StartY=-74.03 StartZ=0 EndX=384.95 EndY=-74.03 EndZ=0
    g90: LineSegment [constr] StartX=176.53 StartY=3.175 StartZ=0 EndX=214.63 EndY=3.175 EndZ=0
    g91: LineSegment [constr] StartX=214.63 StartY=3.175 StartZ=0 EndX=265.43 EndY=3.175 EndZ=0
    g92: LineSegment [constr] StartX=367.03 StartY=3.175 StartZ=0 EndX=391.16 EndY=3.175 EndZ=0
    g93: LineSegment [constr] StartX=384.95 StartY=-74.03 StartZ=0 EndX=409.08 EndY=-74.03 EndZ=0
    g94: LineSegment [constr] StartX=384.95 StartY=-74.03 StartZ=0 EndX=384.95 EndY=-35.295 EndZ=0
    g95: LineSegment [constr] StartX=409.08 StartY=-35.295 StartZ=0 EndX=42.05 EndY=-35.295 EndZ=0
    g96: LineSegment [constr] StartX=42.05 StartY=-74.03 StartZ=0 EndX=42.05 EndY=-35.295 EndZ=0
    g97: LineSegment [constr] StartX=409.08 StartY=-74.03 StartZ=0 EndX=409.08 EndY=-35.295 EndZ=0
    g98: LineSegment [constr] StartX=367.03 StartY=3.175 StartZ=0 EndX=367.03 EndY=41.91 EndZ=0
    g99: LineSegment [constr] StartX=367.03 StartY=3.175 StartZ=0 EndX=367.03 EndY=-5.6e-14 EndZ=0
    g100: LineSegment [constr] StartX=384.95 StartY=-74.03 StartZ=0 EndX=384.95 EndY=-77.205 EndZ=0
    g101: LineSegment [constr] StartX=409.08 StartY=-74.03 StartZ=0 EndX=409.08 EndY=-77.205 EndZ=0
    g102: LineSegment [constr] StartX=384.95 StartY=-77.205 StartZ=0 EndX=409.08 EndY=-77.205 EndZ=0
    g103: LineSegment [constr] StartX=409.08 StartY=-35.295 StartZ=0 EndX=409.08 EndY=2.8729 EndZ=0
    g104: LineSegment [constr] StartX=409.08 StartY=-77.205 StartZ=0 EndX=409.08 EndY=-115.373 EndZ=0
    g105: LineSegment [constr] StartX=42.05 StartY=-74.03 StartZ=0 EndX=17.92 EndY=-74.03 EndZ=0
    g106: LineSegment [constr] StartX=17.92 StartY=-74.03 StartZ=0 EndX=17.92 EndY=-35.295 EndZ=0
    g107: LineSegment [constr] StartX=17.92 StartY=-35.295 StartZ=0 EndX=42.05 EndY=-35.295 EndZ=0
    g108: LineSegment [constr] StartX=17.92 StartY=-35.295 StartZ=0 EndX=-8.0772 EndY=-35.295 EndZ=0
    g109: LineSegment [constr] StartX=409.08 StartY=-35.295 StartZ=0 EndX=435.077 EndY=-35.295 EndZ=0
    g110: LineSegment [constr] StartX=314 StartY=-16.25 StartZ=0 EndX=314 EndY=-96.25 EndZ=0
    g111: LineSegment [constr] StartX=113 StartY=-16.25 StartZ=0 EndX=113 EndY=-96.25 EndZ=0
    g112: LineSegment [constr] StartX=113 StartY=-16.25 StartZ=0 EndX=314 EndY=-16.25 EndZ=0
    g113: LineSegment [constr] StartX=113 StartY=-96.25 StartZ=0 EndX=314 EndY=-96.25 EndZ=0
    g114: LineSegment [constr] StartX=106.75 StartY=-2.0081 StartZ=0 EndX=320.25 EndY=-2.0081 EndZ=0
    g115: LineSegment [constr] StartX=106.75 StartY=-110.492 StartZ=0 EndX=320.25 EndY=-110.492 EndZ=0
    g116: Circle CenterX=106.75 CenterY=-2.0081 CenterZ=0 NormalX=0 NormalY=0 NormalZ=1 AngleXU=0 Radius=1.627
    g117: Circle CenterX=106.75 CenterY=-110.492 CenterZ=0 NormalX=0 NormalY=0 NormalZ=1 AngleXU=0 Radius=1.627
    g118: Circle CenterX=320.25 CenterY=-110.492 CenterZ=0 NormalX=0 NormalY=0 NormalZ=1 AngleXU=0 Radius=1.627
    g119: Circle CenterX=320.25 CenterY=-2.0081 CenterZ=0 NormalX=0 NormalY=0 NormalZ=1 AngleXU=0 Radius=1.627
    g120: LineSegment [constr] StartX=286.179 StartY=2.8729 StartZ=0 EndX=354.321 EndY=2.8729 EndZ=0
    g121: LineSegment [constr] StartX=320.25 StartY=-3.6351 StartZ=0 EndX=320.25 EndY=-110.492 EndZ=0
    g122: LineSegment [constr] StartX=320.25 StartY=-0.3811 StartZ=0 EndX=320.25 EndY=2.8729 EndZ=0
    g123: LineSegment [constr] StartX=320.25 StartY=-0.3811 StartZ=0 EndX=320.25 EndY=-3.6351 EndZ=0
    g124: LineSegment [constr] StartX=72.679 StartY=2.8729 StartZ=0 EndX=140.821 EndY=2.8729 EndZ=0
    g125: LineSegment [constr] StartX=106.75 StartY=-2.0081 StartZ=0 EndX=106.75 EndY=-110.492 EndZ=0
    g126: LineSegment [constr] StartX=72.679 StartY=-115.373 StartZ=0 EndX=140.821 EndY=-115.373 EndZ=0
    g127: LineSegment [constr] StartX=286.179 StartY=-115.373 StartZ=0 EndX=354.321 EndY=-115.373 EndZ=0
    g128: LineSegment [constr] StartX=320.25 StartY=-115.373 StartZ=0 EndX=320.25 EndY=-110.492 EndZ=0
    g129: LineSegment [constr] StartX=106.75 StartY=-2.0081 StartZ=0 EndX=106.75 EndY=2.8729 EndZ=0
    g130: LineSegment [constr] StartX=106.75 StartY=-16.25 StartZ=0 EndX=113 EndY=-16.25 EndZ=0
    g131: LineSegment [constr] StartX=314 StartY=-16.25 StartZ=0 EndX=320.25 EndY=-16.25 EndZ=0
    g132: LineSegment [constr] StartX=113 StartY=-16.25 StartZ=0 EndX=113 EndY=-2.0081 EndZ=0
    g133: LineSegment [constr] StartX=113 StartY=-96.25 StartZ=0 EndX=113 EndY=-110.492 EndZ=0
    g134: LineSegment StartX=199.174 StartY=2.8729 StartZ=0 EndX=140.821 EndY=2.8729 EndZ=0
    g135: LineSegment StartX=200.374 StartY=-22.179 StartZ=0 EndX=200.374 EndY=1.6729 EndZ=0
    g136: LineSegment StartX=225.426 StartY=-23.379 StartZ=0 EndX=201.574 EndY=-23.379 EndZ=0
    g137: LineSegment StartX=286.179 StartY=2.8729 StartZ=0 EndX=227.826 EndY=2.8729 EndZ=0
    g138: LineSegment StartX=226.626 StartY=1.6729 StartZ=0 EndX=226.626 EndY=-22.179 EndZ=0
    g139: ArcOfCircle CenterX=199.174 CenterY=1.6729 CenterZ=0 NormalX=0 NormalY=0 NormalZ=1 AngleXU=0 Radius=1.2 StartAngle=1e-16 EndAngle=1.5708
    g140: GeomPoint [constr] X=200.374 Y=2.8729 Z=0
    g141: ArcOfCircle CenterX=201.574 CenterY=-22.179 CenterZ=0 NormalX=0 NormalY=0 NormalZ=1 AngleXU=0 Radius=1.2 StartAngle=3.14159 EndAngle=4.71239
    g142: GeomPoint [constr] X=200.374 Y=-23.379 Z=0
    g143: ArcOfCircle CenterX=225.426 CenterY=-22.179 CenterZ=0 NormalX=0 NormalY=0 NormalZ=1 AngleXU=0 Radius=1.2 StartAngle=4.71239 EndAngle=6.28319
    g144: GeomPoint [constr] X=226.626 Y=-23.379 Z=0
    g145: ArcOfCircle CenterX=227.826 CenterY=1.6729 CenterZ=0 NormalX=0 NormalY=0 NormalZ=1 AngleXU=0 Radius=1.2 StartAngle=1.5708 EndAngle=3.14159
    g146: GeomPoint [constr] X=226.626 Y=2.8729 Z=0
    g147: LineSegment [constr] StartX=213.5 StartY=-115.373 StartZ=0 EndX=213.5 EndY=-23.379 EndZ=0
  constraints (388):
    c: Equal(g1,g0)
    c: Horizontal(g2)
    c: Vertical(g3)
    c: Horizontal(g4)
    c: Vertical(g5)
    c: Vertical(g6)
    c: Horizontal(g7)
    c: Vertical(g8)
    c: Horizontal(g9)
    c: Vertical(g10)
    c: Vertical(g11)
    c: Tangent(g10,g12) = -1.5708
    c: Tangent(g9,g13) = 1.5708
    c: Tangent(g10,g13) = 1.5708
    c: Tangent(g8,g14) = -1.5708
    c: Tangent(g9,g14) = -1.5708
    c: Tangent(g7,g15) = -1.5708
    c: Tangent(g8,g15) = -1.5708
    c: Tangent(g6,g16) = 1.5708
    c: Tangent(g7,g16) = 1.5708
    c: Tangent(g6,g17) = -1.5708
    c: Tangent(g5,g18) = -1.5708
    c: Tangent(g4,g19) = 1.5708
    c: Tangent(g5,g19) = 1.5708
    c: Tangent(g3,g20) = -1.5708
    c: Tangent(g4,g20) = -1.5708
    c: Tangent(g2,g21) = -1.5708
    c: Tangent(g3,g21) = -1.5708
    c: Tangent(g2,g22) = 1.5708
    c: Tangent(g11,g22) = 1.5708
    c: Tangent(g11,g23) = -1.5708
    c: Equal(g12,g13)
    c: Equal(g13,g14)
    c: Equal(g14,g15)
    c: Equal(g15,g16)
    c: Equal(g16,g17)
    c: Equal(g18,g19)
    c: Equal(g19,g20)
    c: Equal(g20,g21)
    c: Equal(g21,g22)
    c: Equal(g22,g23)
    c: Distance(g1,g1) = 0.254
    c: Equal(g5,g11)
    c: Equal(g5,g6)
    c: Equal(g8,g3)
    c: Equal(g11,g10)
    c: Equal(g4,g7)
    c: Radius(g23) = 1.2
    c: Equal(g9,g7)
    c: Tangent(g24,g26) = 1.5708
    c: Tangent(g24,g27) = -1.5708
    c: Tangent(g25,g26) = 1.5708
    c: Tangent(g25,g27) = -1.5708
    c: Equal(g24,g25)
    c: Vertical(g26)
    c: Coincident(g29,g25)
    c: Vertical(g29)
    c: Equal(g28,g29)
    c: Coincident(g28,g24)
    c: Vertical(g28)
    c: PointOnObject(g30,g9)
    c: Vertical(g30)
    c: PointOnObject(g31,g7)
    c: Vertical(g31)
    c: Tangent(g32,g34) = 1.5708
    c: Tangent(g32,g35) = -1.5708
    c: Tangent(g33,g34) = 1.5708
    c: Tangent(g33,g35) = -1.5708
    c: Equal(g32,g33)
    c: Coincident(g32,g30)
    c: Coincident(g33,g31)
    c: Vertical(g34)
    c: Equal(g30,g31)
    c: Equal(g28,g30)
    c: Equal(g32,g24)
    c: PointOnObject(g36,g3)
    c: Coincident(g36,g24)
    c: Horizontal(g36)
    c: Coincident(g37,g32)
    c: PointOnObject(g37,g8)
    c: Horizontal(g37)
    c: Equal(g37,g36)
    c: Distance(g36,g36) = 2.921
    c: DistanceY(g27,g27) = 16
    c: Diameter(g24) = 3.429
    c: Vertical(g1)
    c: Vertical(g0)
    c: Horizontal(g53)
    c: Vertical(g46)
    c: Horizontal(g47)
    c: Vertical(g48)
    c: Vertical(g39)
    c: Horizontal(g40)
    c: Vertical(g41)
    c: Tangent(g41,g42) = 1.5708
    c: Tangent(g38,g42) = 1.5708
    c: Tangent(g40,g43) = -1.5708
    c: Tangent(g41,g43) = -1.5708
    c: Tangent(g39,g44) = -1.5708
    c: Tangent(g40,g44) = -1.5708
    c: Coincident(g134,g45) = 1.5708
    c: Tangent(g39,g45) = 1.5708
    c: Tangent(g48,g49) = 1.5708
    c: Tangent(g47,g50) = -1.5708
    c: Tangent(g48,g50) = -1.5708
    c: Tangent(g46,g51) = -1.5708
    c: Tangent(g47,g51) = -1.5708
    c: Tangent(g53,g52) = 1.5708
    c: Tangent(g46,g52) = 1.5708
    c: Equal(g42,g43)
    c: Equal(g43,g44)
    c: Equal(g44,g45)
    c: Equal(g45,g49)
    c: Equal(g49,g50)
    c: Equal(g51,g52)
    c: Equal(g50,g51)
    c: Equal(g48,g39)
    c: Horizontal(g38)
    c: Horizontal(g54)
    c: Vertical(g55)
    c: Horizontal(g56)
    c: Vertical(g57)
    c: Horizontal(g58)
    c: Vertical(g59)
    c: Horizontal(g60)
    c: Vertical(g68)
    c: Horizontal(g70)
    c: Tangent(g68,g69) = 1.5708
    c: Tangent(g70,g69) = 1.5708
    c: Tangent(g60,g61) = -1.5708
    c: Tangent(g68,g61) = -1.5708
    c: Tangent(g59,g62) = -1.5708
    c: Tangent(g60,g62) = -1.5708
    c: Tangent(g58,g63) = 1.5708
    c: Tangent(g59,g63) = 1.5708
    c: Tangent(g57,g64) = 1.5708
    c: Tangent(g58,g64) = 1.5708
    c: Tangent(g56,g65) = -1.5708
    c: Tangent(g57,g65) = -1.5708
    c: Tangent(g55,g66) = -1.5708
    c: Tangent(g56,g66) = -1.5708
    c: Tangent(g54,g67) = 1.5708
    c: Tangent(g55,g67) = 1.5708
    c: Equal(g69,g61)
    c: Equal(g61,g62)
    c: Equal(g62,g63)
    c: Equal(g64,g65)
    c: Equal(g65,g66)
    c: Equal(g66,g67)
    c: Equal(g57,g59)
    c: Equal(g54,g70)
    c: Tangent(g17,g70) = -1.5708
    c: Tangent(g12,g53) = -1.5708
    c: Tangent(g54,g18) = -1.5708
    c: Tangent(g23,g38) = -1.5708
    c: Coincident(g0,g2)
    c: Coincident(g1,g4)
    c: PointOnObject(g29,g4)
    c: PointOnObject(g28,g2)
    c: Coincident(g0,g-4)
    c: Coincident(g-4,g1)
    c: Equal(g23,g42)
    c: Equal(g18,g67)
    c: Equal(g63,g64)
    c: Coincident(g71,g41)
    c: Horizontal(g71)
    c: Equal(g71,g0)
    c: Coincident(g72,g39)
    c: Equal(g71,g72)
    c: Coincident(g73,g48)
    c: Coincident(g74,g46)
    c: Horizontal(g74)
    c: Equal(g74,g73)
    c: Equal(g73,g72)
    c: Distance(g73,g73) = 0.254
    c: Distance(g74,g74) = 0.254
    c: Distance(g72,g72) = 0.254
    c: Distance(g71,g71) = 0.254
    c: Distance(g0,g0) = 0.254
    c: Equal(g54,g38)
    c: Coincident(g74,g-6)
    c: Coincident(g73,g-6)
    c: Coincident(g72,g-5)
    c: Coincident(g71,g-5)
    c: Equal(g55,g41)
    c: Equal(g57,g55)
    c: Equal(g56,g40)
    c: Equal(g60,g47)
    c: Equal(g59,g68)
    c: Distance(g26,g-3) = 0.127
    c: PointOnObject(g41,g-8)
    c: DistanceX(g47,g47) = 63.342
    c: DistanceX(g40,g40) = 63.342
    c: DistanceY(g3,g3) = 63.342
    c: Equal(g82,g81)
    c: Equal(g81,g80)
    c: Equal(g80,g75)
    c: Equal(g75,g76)
    c: Equal(g76,g77)
    c: Equal(g77,g78)
    c: Equal(g78,g79)
    c: Coincident(g83,g82)
    c: Coincident(g83,g81)
    c: Horizontal(g83)
    c: Coincident(g84,g81)
    c: Coincident(g84,g80)
    c: Coincident(g85,g80)
    c: Coincident(g85,g75)
    c: Coincident(g86,g75)
    c: Coincident(g86,g76)
    c: Horizontal(g86)
    c: Coincident(g87,g76)
    c: Coincident(g87,g77)
    c: Coincident(g88,g77)
    c: Coincident(g88,g78)
    c: Horizontal(g88)
    c: Coincident(g89,g78)
    c: Coincident(g89,g79)
    c: Horizontal(g89)
    c: Horizontal(g87)
    c: Horizontal(g85)
    c: Horizontal(g84)
    c: Equal(g83,g84)
    c: Equal(g84,g85)
    c: Equal(g85,g87)
    c: Equal(g87,g88)
    c: Equal(g88,g89)
    c: Coincident(g90,g-9)
    c: Coincident(g90,g-10)
    c: Coincident(g91,g90)
    c: Coincident(g91,g-11)
    c: Equal(g90,g86)
    c: Equal(g91,g87)
    c: Coincident(g92,g-14)
    c: PointOnObject(g92,g-13)
    c: Horizontal(g92)
    c: Coincident(g93,g79)
    c: Horizontal(g93)
    c: Coincident(g94,g79)
    c: Vertical(g94)
    c: Horizontal(g95)
    c: Coincident(g96,g82)
    c: Coincident(g96,g95)
    c: Vertical(g96)
    c: Coincident(g97,g93)
    c: Coincident(g97,g95)
    c: Vertical(g97)
    c: PointOnObject(g94,g95)
    c: Coincident(g98,g92)
    c: PointOnObject(g98,g-12)
    c: Vertical(g98)
    c: Equal(g98,g94)
    c: Equal(g93,g92)
    c: Coincident(g99,g92)
    c: PointOnObject(g99,g-15)
    c: Vertical(g99)
    c: Coincident(g100,g79)
    c: Coincident(g101,g93)
    c: Vertical(g101)
    c: Coincident(g102,g100)
    c: Coincident(g102,g101)
    c: Vertical(g100)
    c: Horizontal(g102)
    c: Equal(g100,g99)
    c: Coincident(g103,g95)
    c: PointOnObject(g103,g53)
    c: Vertical(g103)
    c: Coincident(g104,g101)
    c: PointOnObject(g104,g70)
    c: Vertical(g104)
    c: Equal(g104,g103)
    c: Coincident(g105,g82)
    c: Horizontal(g105)
    c: Coincident(g106,g105)
    c: Vertical(g106)
    c: Coincident(g107,g95)
    c: Horizontal(g107)
    c: Coincident(g107,g106)
    c: Coincident(g108,g106)
    c: PointOnObject(g108,g3)
    c: Horizontal(g108)
    c: Coincident(g109,g95)
    c: PointOnObject(g109,g8)
    c: Horizontal(g109)
    c: Equal(g109,g108)
    c: Equal(g105,g93)
    c: DistanceX(g85,g85) = 50.8
    c: DistanceX(g86,g86) = 38.1
    c: Diameter(g80) = 3.254
    c: Vertical(g110)
    c: Vertical(g111)
    c: Coincident(g112,g111)
    c: Coincident(g112,g110)
    c: Coincident(g113,g111)
    c: Coincident(g113,g110)
    c: Horizontal(g113)
    c: Equal(g112,g-17)
    c: Equal(g110,g-16)
    c: Horizontal(g114)
    c: Horizontal(g115)
    c: Coincident(g117,g115)
    c: Coincident(g118,g115)
    c: Equal(g119,g118)
    c: Equal(g118,g117)
    c: Equal(g116,g117)
    c: Equal(g116,g80)
    c: Coincident(g120,g137)
    c: Coincident(g120,g52)
    c: Coincident(g121,g115)
    c: Vertical(g121)
    c: PointOnObject(g122,g119)
    c: PointOnObject(g122,g120)
    c: PointOnObject(g121,g119)
    c: Tangent(g121,g122)
    c: Coincident(g123,g122)
    c: Coincident(g123,g121)
    c: PointOnObject(g119,g123)
    c: Equal(g123,g122)
    c: Coincident(g114,g119)
    c: Equal(g114,g115)
    c: Coincident(g124,g38)
    c: Tangent(g124,g45) = -1.5708
    c: Coincident(g125,g115)
    c: Coincident(g126,g54)
    c: Coincident(g126,g58)
    c: Vertical(g128)
    c: Coincident(g128,g115)
    c: Symmetric(g127,g127,g128)
    c: Coincident(g127,g58)
    c: Coincident(g127,g69)
    c: Coincident(g125,g116)
    c: Coincident(g114,g116)
    c: Coincident(g129,g114)
    c: Symmetric(g124,g124,g129)
    c: Vertical(g129)
    c: Equal(g129,g128)
    c: PointOnObject(g130,g125)
    c: Coincident(g130,g111)
    c: Horizontal(g130)
    c: Coincident(g131,g110)
    c: PointOnObject(g131,g121)
    c: Horizontal(g131)
    c: Equal(g131,g130)
    c: Coincident(g132,g111)
    c: PointOnObject(g132,g114)
    c: Vertical(g132)
    c: Coincident(g133,g111)
    c: PointOnObject(g133,g115)
    c: Vertical(g133)
    c: Equal(g133,g132)
    c: Horizontal(g112)
    c: Horizontal(g134)
    c: Horizontal(g137)
    c: Vertical(g135)
    c: Vertical(g138)
    c: PointOnObject(g140,g134)
    c: PointOnObject(g140,g135)
    c: Tangent(g134,g139) = -1.5708
    c: Tangent(g135,g139) = -1.5708
    c: PointOnObject(g142,g135)
    c: PointOnObject(g142,g136)
    c: Tangent(g135,g141) = 1.5708
    c: Tangent(g136,g141) = 1.5708
    c: PointOnObject(g144,g136)
    c: PointOnObject(g144,g138)
    c: Tangent(g136,g143) = 1.5708
    c: Tangent(g138,g143) = 1.5708
    c: PointOnObject(g146,g137)
    c: PointOnObject(g146,g138)
    c: Tangent(g137,g145) = -1.5708
    c: Tangent(g138,g145) = -1.5708
    c: Equal(g145,g143)
    c: Equal(g143,g141)
    c: Equal(g139,g141)
    c: Equal(g139,g45)
    c: Symmetric(g58,g58,g147)
    c: Symmetric(g136,g136,g147)
    c: Vertical(g147)
    c: PointOnObject(g39,g-5)
    c: PointOnObject(g48,g-6)
    c: Tangent(g49,g120) = -1.5708
    c: Equal(g134,g137)
    c: Equal(g136,g138)
    c: Tangent(g136,g9)
    c: Distance(g8,g-2) = 435.077  'DeltaX'
    c: Distance(g60,g-1) = 119.627  'DeltaY'
    c: Distance(g3,g-2) = 8.0772  'OffsetX'
    c: Distance(g47,g-1) = 7.1271  'OffsetY'
FEATURE [PartDesign::Pad] Pad
  Direction = (0,-1,2e-16)
  Length = 1.8542
  Length2 = 10
  Placement = pos=(0,127.227,2.73e-14) rot=(1,0,0;1.5708rad)
  Profile = -> Sketch
  ReferenceAxis = -> Sketch [N_Axis]
  Refine = true
  Suppressed = false
  Type = 0
  expr: Length = <<dimensions>>#VarSet.EnclosureTotalThickness
FEATURE [PartDesign::Body] Body  label="PanelBack"
  AllowCompound = false
  Group = -> [Sketch,Pad,Binder001,Binder,Binder002,Binder003]
  Origin = -> Origin
  Tip = -> Pad
COMPONENT P8 — recipe-attached ("PanelSide", a linked part whose construction recipe lives in a companion FreeCAD document of the same project; that document's serialized recipe follows).
Construction recipe (the companion document, serialized — sketch geometry with constraints, then the solid features built on it; lengths are millimeters unless a unit is written):

FCSTD DOCUMENT  (FreeCAD 1.0R38641 +468 (Git))
Label: panel_side
License: All rights reserved
LicenseURL: https://en.wikipedia.org/wiki/All_rights_reserved
objects: PartDesign::SubShapeBinder×1, Sketcher::SketchObject×1, PartDesign::Pad×1, PartDesign::Body×1
note: 7 computed .brp shape members not serialized (recipe doc carries the construction recipe); baked Part::Feature solids carry a one-line shape summary decoded from their .brp
EXTERNAL_REF file=dimensions.FCStd obj=VarSet
EXTERNAL_REF file=../third_party/tiptop_z_rail.FCStd obj=Body

FEATURE [PartDesign::SubShapeBinder] Binder001  label="RailBinder"
  BindCopyOnChange = 0
  BindMode = 0
  ClaimChildren = false
  Context = -> Body001 [Binder001.]
  Fuse = false
  MakeFace = true
  OffsetFill = false
  OffsetIntersection = false
  OffsetJoinType = 0
  OffsetOpenResult = false
  PartialLoad = false
  Refine = true
  Relative = true
  Support = -> [<external ../third_party/tiptop_z_rail.FCStd>#Body]
  _Version = 2
FEATURE [Sketcher::SketchObject] Sketch
  ArcFitTolerance = 1e-06
  AttachmentSupport = -> [Binder001]
  ExternalGeometry = -> [Binder001]
  FullyConstrained = true
  MakeInternals = false
  MapMode = 5
  Placement = pos=(1e-15,0,0) rot=(0.57735,0.57735,0.57735;2.0944rad)
  expr: .Constraints.CornerRadius = <<dimensions>>#VarSet.EnclosureCornerRadius
  expr: .Constraints.MaxBoltNutOuterDiameter = dimensions#VarSet.EnclosureFrameHoleDiameter + dimensions#VarSet.FrameMinWidth + 2 * dimensions#VarSet.FrameFinishThickness
  expr: Constraints[21] = <<dimensions>>#VarSet.EnclosureFrameHoleDiameter
  expr: Constraints[61] = 122.5
  expr: Constraints[63] = <<dimensions>>#VarSet.EnclosureTotalThickness + 2 * <<dimensions>>#VarSet.EnclosureFinishThickness
  expr: Constraints[71] = <<dimensions>>#VarSet.EnclosureRailHoleDiameter
  sketch-geometry (32):
    g0: LineSegment [constr] StartX=-1.2 StartY=-56.25 StartZ=0 EndX=131.3 EndY=-56.25 EndZ=0
    g1: Circle CenterX=14.3 CenterY=5 CenterZ=0 NormalX=0 NormalY=0 NormalZ=1 AngleXU=0 Radius=2.127
    g2: Circle CenterX=14.3 CenterY=-117.5 CenterZ=0 NormalX=0 NormalY=0 NormalZ=1 AngleXU=0 Radius=2.127
    g3: LineSegment [constr] StartX=14.3 StartY=5 StartZ=0 EndX=31.925 EndY=5 EndZ=0
    g4: LineSegment StartX=31.925 StartY=3.9459 StartZ=0 EndX=98.175 EndY=3.9459 EndZ=0
    g5: LineSegment StartX=98.175 StartY=6.0541 StartZ=0 EndX=31.925 EndY=6.0541 EndZ=0
    g6: LineSegment [constr] StartX=65.05 StartY=10 StartZ=0 EndX=65.05 EndY=-122.5 EndZ=0
    g7: LineSegment StartX=4.7e-14 StartY=10 StartZ=0 EndX=130.1 EndY=10 EndZ=0
    g8: ArcOfCircle CenterX=4.69e-14 CenterY=8.8 CenterZ=0 NormalX=0 NormalY=0 NormalZ=1 AngleXU=0 Radius=1.2 StartAngle=1.5708 EndAngle=3.14159
    g9: ArcOfCircle CenterX=130.1 CenterY=8.8 CenterZ=0 NormalX=0 NormalY=0 NormalZ=1 AngleXU=0 Radius=1.2 StartAngle=-9e-16 EndAngle=1.5708
    g10: LineSegment StartX=131.3 StartY=8.8 StartZ=0 EndX=131.3 EndY=-121.3 EndZ=0
    g11: LineSegment StartX=-1.2 StartY=8.8 StartZ=0 EndX=-1.2 EndY=-121.3 EndZ=0
    g12: LineSegment StartX=4.65e-14 StartY=-122.5 StartZ=0 EndX=130.1 EndY=-122.5 EndZ=0
    g13: ArcOfCircle CenterX=4.67e-14 CenterY=-121.3 CenterZ=0 NormalX=0 NormalY=0 NormalZ=1 AngleXU=0 Radius=1.2 StartAngle=3.14159 EndAngle=4.71239
    g14: ArcOfCircle CenterX=130.1 CenterY=-121.3 CenterZ=0 NormalX=0 NormalY=0 NormalZ=1 AngleXU=0 Radius=1.2 StartAngle=4.71239 EndAngle=6.28319
    g15: LineSegment [constr] StartX=31.925 StartY=6.0541 StartZ=0 EndX=31.925 EndY=10 EndZ=0
    g16: Circle CenterX=56.923 CenterY=-56.25 CenterZ=0 NormalX=0 NormalY=0 NormalZ=1 AngleXU=0 Radius=3.127
    g17: Circle CenterX=73.177 CenterY=-56.25 CenterZ=0 NormalX=0 NormalY=0 NormalZ=1 AngleXU=0 Radius=3.127
    g18: Circle [constr] CenterX=56.923 CenterY=-56.25 CenterZ=0 NormalX=0 NormalY=0 NormalZ=1 AngleXU=0 Radius=8.127
    g19: ArcOfCircle CenterX=31.925 CenterY=5 CenterZ=0 NormalX=0 NormalY=0 NormalZ=1 AngleXU=0 Radius=1.0541 StartAngle=1.5708 EndAngle=4.71239
    g20: ArcOfCircle CenterX=98.175 CenterY=5 CenterZ=0 NormalX=0 NormalY=0 NormalZ=1 AngleXU=0 Radius=1.0541 StartAngle=4.71239 EndAngle=7.85398
    g21: ArcOfCircle CenterX=126.3 CenterY=-23.125 CenterZ=0 NormalX=0 NormalY=0 NormalZ=1 AngleXU=0 Radius=1.0541 StartAngle=-9e-16 EndAngle=3.14159
    g22: ArcOfCircle CenterX=126.3 CenterY=-89.375 CenterZ=0 NormalX=0 NormalY=0 NormalZ=1 AngleXU=0 Radius=1.0541 StartAngle=3.14159 EndAngle=6.28319
    g23: LineSegment StartX=127.354 StartY=-23.125 StartZ=0 EndX=127.354 EndY=-89.375 EndZ=0
    g24: LineSegment StartX=125.246 StartY=-23.125 StartZ=0 EndX=125.246 EndY=-89.375 EndZ=0
    g25: LineSegment [constr] StartX=127.354 StartY=-23.125 StartZ=0 EndX=131.3 EndY=-23.125 EndZ=0
    g26: LineSegment [constr] StartX=31.925 StartY=-122.5 StartZ=0 EndX=31.925 EndY=-118.554 EndZ=0
    g27: ArcOfCircle CenterX=31.925 CenterY=-117.5 CenterZ=0 NormalX=0 NormalY=0 NormalZ=1 AngleXU=0 Radius=1.0541 StartAngle=1.5708 EndAngle=4.71239
    g28: ArcOfCircle CenterX=98.175 CenterY=-117.5 CenterZ=0 NormalX=0 NormalY=0 NormalZ=1 AngleXU=0 Radius=1.0541 StartAngle=4.71239 EndAngle=7.85398
    g29: LineSegment StartX=31.925 StartY=-116.446 StartZ=0 EndX=98.175 EndY=-116.446 EndZ=0
    g30: LineSegment StartX=31.925 StartY=-118.554 StartZ=0 EndX=98.175 EndY=-118.554 EndZ=0
    g31: LineSegment [constr] StartX=-1.2 StartY=3.9459 StartZ=0 EndX=65.05 EndY=3.9459 EndZ=0
  constraints (76):
    c: Symmetric(g2,g1,g0)
    c: Equal(g1,g2)
    c: Coincident(g3,g1)
    c: Horizontal(g3)
    c: Equal(g8,g9)
    c: Tangent(g9,g10) = 1.5708
    c: Tangent(g7,g9) = 1.5708
    c: Tangent(g13,g11) = -1.5708
    c: Tangent(g13,g12) = -1.5708
    c: Equal(g13,g8)
    c: Tangent(g12,g14) = -1.5708
    c: Tangent(g14,g10) = 1.5708
    c: Equal(g14,g8)
    c: Vertical(g15)
    c: Symmetric(g4,g4,g6)
    c: Horizontal(g5)
    c: Horizontal(g7)
    c: PointOnObject(g16,g0)
    c: PointOnObject(g17,g0)
    c: Equal(g16,g17)
    c: Symmetric(g16,g17,g6)
    c: Diameter(g17) = 6.254
    c: Coincident(g18,g16)
    c: Tangent(g18,g6)
    c: Diameter(g18) = 16.254  'MaxBoltNutOuterDiameter'
    c: Coincident(g19,g3)
    c: Tangent(g5,g19) = -1.5708
    c: Tangent(g4,g19) = -1.5708
    c: Tangent(g5,g20) = -1.5708
    c: Tangent(g4,g20) = -1.5708
    c: Tangent(g21,g23) = 1.5708
    c: Tangent(g21,g24) = -1.5708
    c: Tangent(g22,g23) = 1.5708
    c: Tangent(g22,g24) = -1.5708
    c: Equal(g21,g22)
    c: Symmetric(g22,g21,g0)
    c: Coincident(g15,g5)
    c: Coincident(g25,g21)
    c: Horizontal(g25)
    c: PointOnObject(g25,g10)
    c: Equal(g25,g15)
    c: PointOnObject(g26,g12)
    c: Vertical(g26)
    c: Tangent(g27,g29) = 1.5708
    c: Tangent(g27,g30) = -1.5708
    c: Tangent(g28,g29) = 1.5708
    c: Tangent(g28,g30) = -1.5708
    c: Equal(g27,g28)
    c: Coincident(g26,g27)
    c: Equal(g26,g15)
    c: Equal(g27,g19)
    c: Symmetric(g27,g28,g6)
    c: Vertical(g11)
    c: Tangent(g8,g11) = -1.5708
    c: Tangent(g7,g8) = 1.5708
    c: Symmetric(g8,g11,g0)
    c: Symmetric(g9,g10,g0)
    c: Symmetric(g12,g12,g6)
    c: Symmetric(g7,g7,g6)
    c: Equal(g4,g24)
    c: Equal(g4,g29)
    c: DistanceY(g2,g1) = 122.5
    c: Equal(g7,g11)
    c: Distance(g21,g21) = 2.1082
    c: PointOnObject(g15,g7)
    c: PointOnObject(g31,g11)
    c: Symmetric(g4,g4,g31)
    c: Symmetric(g31,g31,g4)
    c: Radius(g13) = 1.2  'CornerRadius'
    c: Distance(g15,g15) = 3.9459  'EdgeToSlot'
    c: DistanceX(g5,g5) = 66.25  'SlotLength'
    c: Diameter(g1) = 4.254
    c: Equal(g20,g21)
    c: Horizontal(g12)
    c: Coincident(g1,g-3)
    c: Coincident(g-4,g7)
FEATURE [PartDesign::Pad] Pad
  Direction = (1,0,0)
  Length = 1.8542
  Length2 = 10
  Profile = -> Sketch
  ReferenceAxis = -> Sketch [N_Axis]
  Refine = true
  Reversed = true
  Suppressed = false
  Type = 0
  expr: Length = <<dimensions>>#VarSet.EnclosureTotalThickness
FEATURE [PartDesign::Body] Body001  label="PanelSide"
  AllowCompound = false
  Group = -> [Sketch,Pad,Binder001]
  Origin = -> Origin001
  Tip = -> Pad
COMPONENT P9 — same part as P8; its construction recipe is shown at P8.
COMPONENT P10 — recipe-attached ("PanelTopAndBottom", a linked part whose construction recipe lives in a companion FreeCAD document of the same project; that document's serialized recipe follows).
Construction recipe (the companion document, serialized — sketch geometry with constraints, then the solid features built on it; lengths are millimeters unless a unit is written):

FCSTD DOCUMENT  (FreeCAD 1.0R38641 +468 (Git))
Label: panel_top_and_bottom
License: All rights reserved
LicenseURL: https://en.wikipedia.org/wiki/All_rights_reserved
objects: PartDesign::SubShapeBinder×2, Sketcher::SketchObject×1, PartDesign::Pad×1, PartDesign::Body×1
note: 8 computed .brp shape members not serialized (recipe doc carries the construction recipe); baked Part::Feature solids carry a one-line shape summary decoded from their .brp
EXTERNAL_REF file=dimensions.FCStd obj=VarSet
EXTERNAL_REF file=panel_side.FCStd obj=Sketch
EXTERNAL_REF file=panel_side.FCStd obj=Body001
EXTERNAL_REF file=../third_party/tiptop_z_rail.FCStd obj=Body

FEATURE [PartDesign::SubShapeBinder] Binder  label="SidePanelBinder"
  BindCopyOnChange = 0
  BindMode = 0
  ClaimChildren = false
  Context = -> Body [Binder.]
  Fuse = false
  MakeFace = true
  OffsetFill = false
  OffsetIntersection = false
  OffsetJoinType = 0
  OffsetOpenResult = false
  PartialLoad = false
  Refine = true
  Relative = true
  Support = -> [<external panel_side.FCStd>#Body001]
  _Version = 2
FEATURE [PartDesign::SubShapeBinder] Binder001  label="RailBinder"
  BindCopyOnChange = 0
  BindMode = 0
  ClaimChildren = false
  Context = -> Body [Binder001.]
  Fuse = false
  MakeFace = true
  OffsetFill = false
  OffsetIntersection = false
  OffsetJoinType = 0
  OffsetOpenResult = false
  PartialLoad = false
  Refine = true
  Relative = true
  Support = -> [<external ../third_party/tiptop_z_rail.FCStd>#Body]
  _Version = 2
FEATURE [Sketcher::SketchObject] Sketch
  ArcFitTolerance = 1e-06
  AttachmentOffset = pos=(0,0,0.127) rot=(0,0,1;0rad)
  AttachmentSupport = -> [Binder,Binder001]
  ExternalGeometry = -> [Binder,Binder001]
  FullyConstrained = true
  MakeInternals = false
  MapMode = 5
  Placement = pos=(0,1.3e-15,4.0729) rot=(0,0,1;0rad)
  expr: .AttachmentOffset.Base.z = dimensions#VarSet.EnclosureFinishThickness
  expr: Constraints[102] = dimensions#VarSet.EnclosureFinishThickness
  expr: Constraints[27] = 2 * <<dimensions>>#VarSet.EnclosureFinishThickness
  expr: Constraints[78] = <<dimensions>>#VarSet.EnclosureTotalThickness + 2 * <<dimensions>>#VarSet.EnclosureFinishThickness
  expr: Constraints[87] = <<dimensions>>#VarSet.EnclosureCornerRadius
  expr: Constraints[89] = panel_side#<<Sketch>>.Constraints.EdgeToSlot
  expr: Constraints[90] = panel_side#<<Sketch>>.Constraints.SlotLength
  sketch-geometry (44):
    g0: LineSegment StartX=-3.0542 StartY=96.721 StartZ=0 EndX=-3.0542 EndY=33.379 EndZ=0
    g1: LineSegment StartX=430.054 StartY=33.379 StartZ=0 EndX=430.054 EndY=96.721 EndZ=0
    g2: ArcOfCircle CenterX=-1.8542 CenterY=96.721 CenterZ=0 NormalX=0 NormalY=0 NormalZ=1 AngleXU=0 Radius=1.2 StartAngle=1.5708 EndAngle=3.14159
    g3: ArcOfCircle CenterX=-1.8542 CenterY=33.379 CenterZ=0 NormalX=0 NormalY=0 NormalZ=1 AngleXU=0 Radius=1.2 StartAngle=3.14159 EndAngle=4.71239
    g4: ArcOfCircle CenterX=428.854 CenterY=33.379 CenterZ=0 NormalX=0 NormalY=0 NormalZ=1 AngleXU=0 Radius=1.2 StartAngle=4.71239 EndAngle=6.28319
    g5: ArcOfCircle CenterX=428.854 CenterY=96.721 CenterZ=0 NormalX=0 NormalY=0 NormalZ=1 AngleXU=0 Radius=1.2 StartAngle=-4.4e-15 EndAngle=1.5708
    g6: LineSegment StartX=2.4 StartY=17.927 StartZ=0 EndX=424.6 EndY=17.927 EndZ=0
    g7: LineSegment StartX=424.6 StartY=131.3 StartZ=0 EndX=2.4 EndY=131.3 EndZ=0
    g8: ArcOfCircle CenterX=2.4 CenterY=130.1 CenterZ=0 NormalX=0 NormalY=0 NormalZ=1 AngleXU=0 Radius=1.2 StartAngle=1.5708 EndAngle=3.14159
    g9: ArcOfCircle CenterX=2.4 CenterY=19.127 CenterZ=0 NormalX=0 NormalY=0 NormalZ=1 AngleXU=0 Radius=1.2 StartAngle=3.14159 EndAngle=4.71239
    g10: ArcOfCircle CenterX=424.6 CenterY=19.127 CenterZ=0 NormalX=0 NormalY=0 NormalZ=1 AngleXU=0 Radius=1.2 StartAngle=4.71239 EndAngle=6.28319
    g11: ArcOfCircle CenterX=424.6 CenterY=130.1 CenterZ=0 NormalX=0 NormalY=0 NormalZ=1 AngleXU=0 Radius=1.2 StartAngle=-2.7e-15 EndAngle=1.5708
    g12: LineSegment StartX=428.854 StartY=97.921 StartZ=0 EndX=427 EndY=97.921 EndZ=0
    g13: LineSegment StartX=425.8 StartY=99.121 StartZ=0 EndX=425.8 EndY=130.1 EndZ=0
    g14: LineSegment StartX=425.8 StartY=19.127 StartZ=0 EndX=425.8 EndY=30.979 EndZ=0
    g15: LineSegment StartX=427 StartY=32.179 StartZ=0 EndX=428.854 EndY=32.179 EndZ=0
    g16: LineSegment StartX=-1.8542 StartY=32.179 StartZ=0 EndX=9e-16 EndY=32.179 EndZ=0
    g17: LineSegment StartX=1.2 StartY=30.979 StartZ=0 EndX=1.2 EndY=19.127 EndZ=0
    g18: LineSegment StartX=1.2 StartY=130.1 StartZ=0 EndX=1.2 EndY=99.121 EndZ=0
    g19: LineSegment StartX=1e-15 StartY=97.921 StartZ=0 EndX=-1.8542 EndY=97.921 EndZ=0
    g20: LineSegment [constr] StartX=1e-15 StartY=97.921 StartZ=0 EndX=1e-15 EndY=98.175 EndZ=0
    g21: LineSegment [constr] StartX=1e-15 StartY=32.179 StartZ=0 EndX=1e-15 EndY=31.925 EndZ=0
    g22: ArcOfCircle CenterX=1.2e-15 CenterY=99.121 CenterZ=0 NormalX=0 NormalY=0 NormalZ=1 AngleXU=0 Radius=1.2 StartAngle=4.71239 EndAngle=6.28319
    g23: ArcOfCircle CenterX=9e-16 CenterY=30.979 CenterZ=0 NormalX=0 NormalY=0 NormalZ=1 AngleXU=0 Radius=1.2 StartAngle=-9e-16 EndAngle=1.5708
    g24: ArcOfCircle CenterX=427 CenterY=30.979 CenterZ=0 NormalX=0 NormalY=0 NormalZ=1 AngleXU=0 Radius=1.2 StartAngle=1.5708 EndAngle=3.14159
    g25: ArcOfCircle CenterX=427 CenterY=99.121 CenterZ=0 NormalX=0 NormalY=0 NormalZ=1 AngleXU=0 Radius=1.2 StartAngle=3.14159 EndAngle=4.71239
    g26: LineSegment [constr] StartX=427 StartY=97.921 StartZ=0 EndX=427 EndY=32.179 EndZ=0
    g27: LineSegment [constr] StartX=1.2 StartY=30.979 StartZ=0 EndX=425.8 EndY=30.979 EndZ=0
    g28: ArcOfCircle CenterX=73.625 CenterY=126.3 CenterZ=0 NormalX=0 NormalY=0 NormalZ=1 AngleXU=0 Radius=1.0541 StartAngle=1.5708 EndAngle=4.71239
    g29: ArcOfCircle CenterX=139.875 CenterY=126.3 CenterZ=0 NormalX=0 NormalY=0 NormalZ=1 AngleXU=0 Radius=1.0541 StartAngle=4.71239 EndAngle=7.85398
    g30: LineSegment StartX=73.625 StartY=127.354 StartZ=0 EndX=139.875 EndY=127.354 EndZ=0
    g31: LineSegment StartX=73.625 StartY=125.246 StartZ=0 EndX=139.875 EndY=125.246 EndZ=0
    g32: ArcOfCircle CenterX=287.125 CenterY=126.3 CenterZ=0 NormalX=0 NormalY=0 NormalZ=1 AngleXU=0 Radius=1.0541 StartAngle=1.5708 EndAngle=4.71239
    g33: ArcOfCircle CenterX=353.375 CenterY=126.3 CenterZ=0 NormalX=0 NormalY=0 NormalZ=1 AngleXU=0 Radius=1.0541 StartAngle=4.71239 EndAngle=7.85398
    g34: LineSegment StartX=287.125 StartY=127.354 StartZ=0 EndX=353.375 EndY=127.354 EndZ=0
    g35: LineSegment StartX=287.125 StartY=125.246 StartZ=0 EndX=353.375 EndY=125.246 EndZ=0
    g36: LineSegment [constr] StartX=213.5 StartY=131.3 StartZ=0 EndX=213.5 EndY=17.8 EndZ=0
    g37: LineSegment [constr] StartX=73.625 StartY=127.354 StartZ=0 EndX=73.625 EndY=131.3 EndZ=0
    g38: LineSegment [constr] StartX=287.125 StartY=127.354 StartZ=0 EndX=287.125 EndY=131.3 EndZ=0
    g39: LineSegment [constr] StartX=139.875 StartY=126.3 StartZ=0 EndX=213.5 EndY=126.3 EndZ=0
    g40: LineSegment [constr] StartX=213.5 StartY=126.3 StartZ=0 EndX=287.125 EndY=126.3 EndZ=0
    g41: LineSegment [constr] StartX=106.75 StartY=99.121 StartZ=0 EndX=213.5 EndY=99.121 EndZ=0
    g42: LineSegment [constr] StartX=106.75 StartY=125.246 StartZ=0 EndX=106.75 EndY=99.121 EndZ=0
    g43: LineSegment [constr] StartX=0 StartY=131.3 StartZ=0 EndX=2.4 EndY=131.3 EndZ=0
  constraints (109):
    c: Tangent(g0,g2) = -1.5708
    c: Tangent(g0,g3) = -1.5708
    c: Tangent(g1,g4) = -1.5708
    c: Tangent(g1,g5) = -1.5708
    c: Vertical(g0)
    c: Vertical(g1)
    c: Equal(g2,g3)
    c: Equal(g3,g4)
    c: Equal(g4,g5)
    c: Tangent(g6,g9) = -1.5708
    c: Tangent(g6,g10) = -1.5708
    c: Tangent(g7,g11) = -1.5708
    c: Tangent(g7,g8) = -1.5708
    c: Horizontal(g6)
    c: Horizontal(g7)
    c: Equal(g8,g9)
    c: Equal(g9,g10)
    c: Equal(g10,g11)
    c: Horizontal(g12)
    c: Vertical(g13)
    c: Vertical(g14)
    c: Horizontal(g15)
    c: Horizontal(g16)
    c: Vertical(g17)
    c: Vertical(g18)
    c: Horizontal(g19)
    c: Equal(g21,g20)
    c: Distance(g20,g20) = 0.254
    c: Tangent(g18,g22) = 1.5708
    c: Tangent(g19,g22) = 1.5708
    c: Tangent(g16,g23) = 1.5708
    c: Tangent(g17,g23) = 1.5708
    c: Tangent(g14,g24) = 1.5708
    c: Tangent(g15,g24) = 1.5708
    c: Tangent(g4,g15) = -1.5708
    c: Tangent(g5,g12) = -1.5708
    c: Tangent(g12,g25) = 1.5708
    c: Tangent(g13,g25) = 1.5708
    c: Tangent(g11,g13) = -1.5708
    c: Tangent(g8,g18) = -1.5708
    c: Tangent(g2,g19) = -1.5708
    c: Tangent(g3,g16) = -1.5708
    c: Tangent(g9,g17) = -1.5708
    c: Tangent(g10,g14) = -1.5708
    c: Equal(g22,g23)
    c: Equal(g23,g24)
    c: Equal(g24,g25)
    c: Equal(g2,g22)
    c: Equal(g22,g8)
    c: Coincident(g26,g12)
    c: Coincident(g26,g15)
    c: Vertical(g26)
    c: Coincident(g27,g17)
    c: Coincident(g27,g14)
    c: Horizontal(g27)
    c: Equal(g12,g19)
    c: Coincident(g16,g21)
    c: Coincident(g19,g20)
    c: Tangent(g28,g30) = 1.5708
    c: Tangent(g28,g31) = -1.5708
    c: Tangent(g29,g30) = 1.5708
    c: Tangent(g29,g31) = -1.5708
    c: Equal(g28,g29)
    c: Horizontal(g30)
    c: Tangent(g32,g34) = 1.5708
    c: Tangent(g32,g35) = -1.5708
    c: Tangent(g33,g34) = 1.5708
    c: Tangent(g33,g35) = -1.5708
    c: Equal(g32,g33)
    c: Horizontal(g34)
    c: Symmetric(g7,g7,g36)
    c: Coincident(g37,g28)
    c: Vertical(g37)
    c: Coincident(g38,g32)
    c: PointOnObject(g38,g7)
    c: Vertical(g38)
    c: Equal(g30,g34)
    c: Equal(g32,g29)
    c: Distance(g28,g28) = 2.1082
    c: Coincident(g39,g29)
    c: PointOnObject(g39,g36)
    c: Horizontal(g39)
    c: Coincident(g40,g39)
    c: Coincident(g40,g32)
    c: PointOnObject(g41,g36)
    c: Symmetric(g31,g31,g42)
    c: Vertical(g42)
    c: Radius(g8) = 1.2
    c: PointOnObject(g37,g7)
    c: Distance(g37,g37) = 3.9459
    c: DistanceX(g30,g30) = 66.25
    c: Symmetric(g22,g41,g41)
    c: Coincident(g42,g41)
    c: Horizontal(g41)
    c: Equal(g1,g0)
    c: Coincident(g43,g7)
    c: Horizontal(g43)
    c: Vertical(g20)
    c: Vertical(g21)
    c: Coincident(g20,g-3)
    c: Coincident(g21,g-3)
    c: PointOnObject(g3,g-4)
    c: Distance(g6,g-5) = 0.127
    c: Coincident(g43,g-6)
    c: Symmetric(g-5,g-5,g36)
    c: Horizontal(g40)
    c: Vertical(g36)
    c: Equal(g39,g40)
    c: DistanceY(g0,g0) = 63.342
FEATURE [PartDesign::Pad] Pad
  Direction = (0,0,1)
  Length = 1.8542
  Length2 = 10
  Placement = pos=(0,1.3e-15,4.0729) rot=(0,0,1;0rad)
  Profile = -> Sketch
  ReferenceAxis = -> Sketch [N_Axis]
  Refine = true
  Suppressed = false
  Type = 0
  expr: Length = <<dimensions>>#VarSet.EnclosureTotalThickness
FEATURE [PartDesign::Body] Body  label="PanelTopAndBottom"
  AllowCompound = false
  Group = -> [Sketch,Pad,Binder,Binder001]
  Origin = -> Origin
  Tip = -> Pad
COMPONENT P11 — same part as P10; its construction recipe is shown at P10.
COMPONENT P12 — geometry summary ("ZRail84Hp"; no construction recipe available for this part):
  bounding box: 427.0 x 23.8 x 10.0 mm
  tessellated surface: 324 triangles
  volume: 44781 mm^3 (44% of its bounding box)
  symmetry: mirror-symmetric across its x mid-plane
COMPONENT P13 — geometry summary ("ZRail84Hp001"; no construction recipe available for this part):
  bounding box: 427.0 x 23.8 x 10.0 mm
  tessellated surface: 324 triangles
  volume: 44781 mm^3 (44% of its bounding box)
  symmetry: mirror-symmetric across its x mid-plane
PROVENANCE & LICENSES
A FreeCAD (.FCStd) document from a public repository crawl; recipes are the document's own serialized feature recipes (and, for linked parts, companion documents' recipes).
License: cc-by-sa-4.0.
